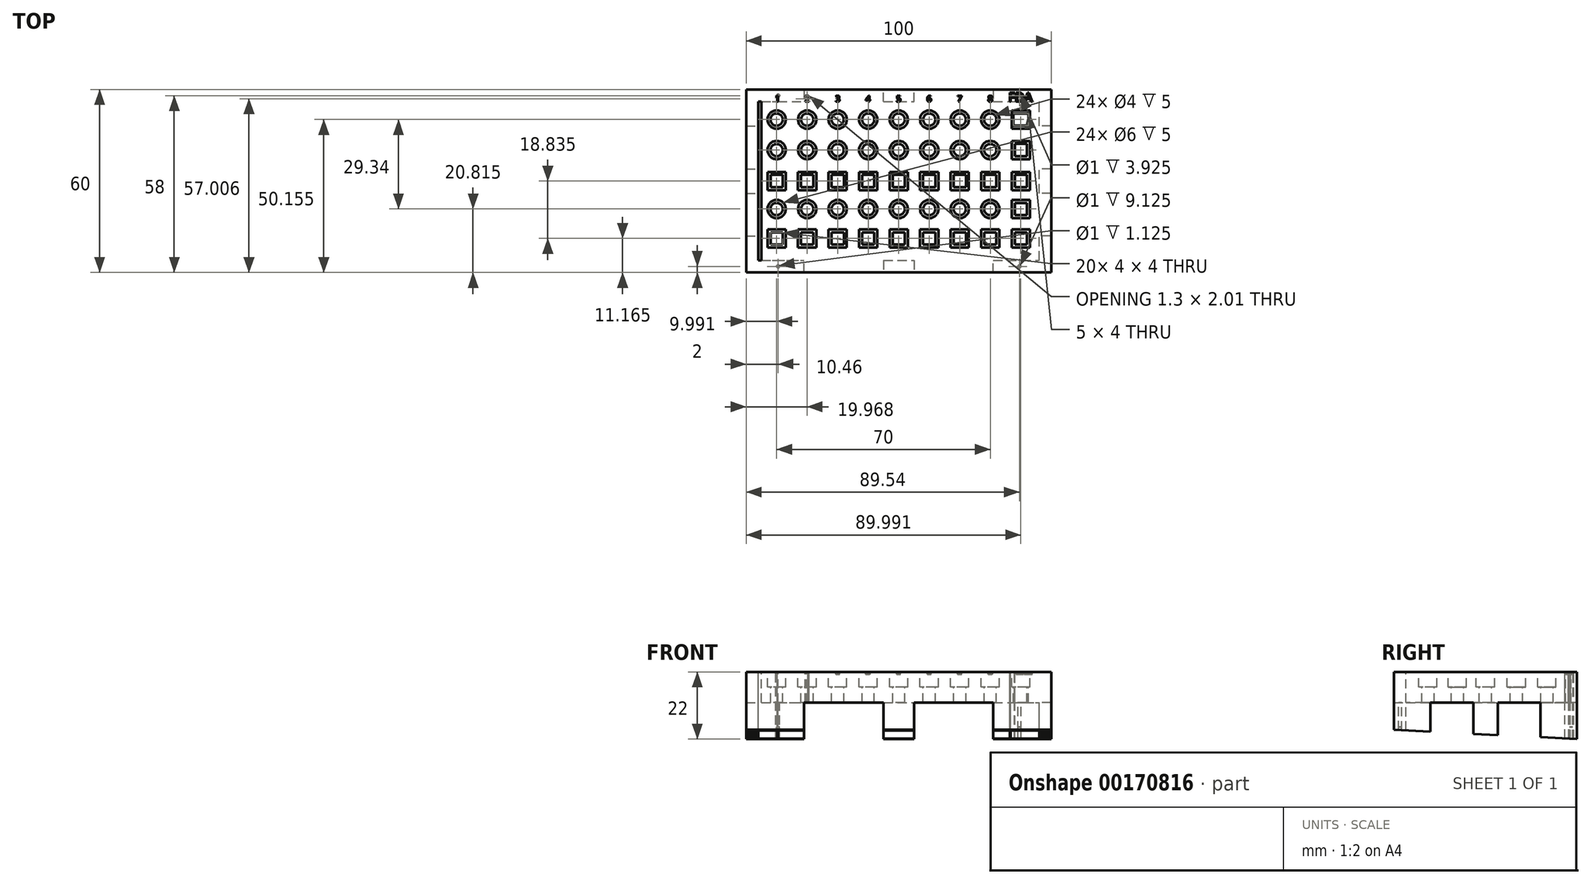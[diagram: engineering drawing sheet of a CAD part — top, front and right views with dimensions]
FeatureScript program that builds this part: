
annotation { "Feature Type Name" : "Feature", "Feature Type Description" : "" }
export const myFeature = defineFeature(function(context is Context, id is Id, definition is map)
    precondition{}
    {
        {
            var Q0;
            Q0=qCreatedBy(makeId("Top.planeOp"),FACE);
            var sketch = newSketch(context, id + "F0", { "sketchPlane" : qUnion([Q0])});
            skLineSegment(sketch, "E0.bottom", {"start": v(0, 0) * mm, "end": v(100, 0) * mm});
            skLineSegment(sketch, "E0.top", {"start": v(0, 60) * mm, "end": v(100, 60) * mm});
            skLineSegment(sketch, "E0.left", {"start": v(0, 0) * mm, "end": v(0, 60) * mm});
            skLineSegment(sketch, "E0.right", {"start": v(100, 0) * mm, "end": v(100, 60) * mm});
            skLineSegment(sketch, "E1.top", {"start": v(0, 88.72) * mm, "end": v(100, 88.72) * mm, "construction": true});
            skLineSegment(sketch, "E1.left", {"start": v(0, 60) * mm, "end": v(0, 88.72) * mm, "construction": true});
            skLineSegment(sketch, "E1.right", {"start": v(100, 60) * mm, "end": v(100, 88.72) * mm, "construction": true});
            skLineSegment(sketch, "E2", {"start": v(5, 88.72) * mm, "end": v(5, 60) * mm, "construction": true});
            skCircle(sketch, "E3", {"center": v(10, 20.81) * mm, "radius": 3 * mm});
            skLineSegment(sketch, "E4.0", {"start": v(4, 56) * mm, "end": v(96, 56) * mm});
            skLineSegment(sketch, "E4.2", {"start": v(4, 4) * mm, "end": v(96, 4) * mm});
            skLineSegment(sketch, "E4.3", {"start": v(96, 4) * mm, "end": v(96, 56) * mm});
            skLineSegment(sketch, "E5.bottom", {"start": v(5, 56) * mm, "end": v(4, 56) * mm});
            skLineSegment(sketch, "E5.top", {"start": v(5, 4.3) * mm, "end": v(4, 4.3) * mm, "construction": true});
            skLineSegment(sketch, "E5.left", {"start": v(5, 56) * mm, "end": v(5, 4.3) * mm});
            skLineSegment(sketch, "E5.right", {"start": v(4, 56) * mm, "end": v(4, 4.3) * mm});
            skPoint(sketch, "E5.middle", {"position": v(4.5, 30.15) * mm});
            skCircle(sketch, "E6", {"center": v(10, 50.15) * mm, "radius": 3 * mm});
            skCircle(sketch, "E7", {"center": v(10, 40.15) * mm, "radius": 3 * mm});
            skLineSegment(sketch, "E8.bottom", {"start": v(13, 14.17) * mm, "end": v(7, 14.17) * mm});
            skLineSegment(sketch, "E8.top", {"start": v(13, 8.17) * mm, "end": v(7, 8.17) * mm});
            skLineSegment(sketch, "E8.left", {"start": v(13, 14.17) * mm, "end": v(13, 8.17) * mm});
            skLineSegment(sketch, "E8.right", {"start": v(7, 14.17) * mm, "end": v(7, 8.17) * mm});
            skLineSegment(sketch, "E9.bottom", {"start": v(12, 13.17) * mm, "end": v(8, 13.17) * mm});
            skLineSegment(sketch, "E9.top", {"start": v(12, 9.17) * mm, "end": v(8, 9.17) * mm});
            skLineSegment(sketch, "E9.left", {"start": v(12, 13.17) * mm, "end": v(12, 9.17) * mm});
            skLineSegment(sketch, "E9.right", {"start": v(8, 13.17) * mm, "end": v(8, 9.17) * mm});
            skPoint(sketch, "E9.middle", {"position": v(10, 11.17) * mm});
            skCircle(sketch, "E10", {"center": v(10, 50.15) * mm, "radius": 2 * mm});
            skCircle(sketch, "E11", {"center": v(10, 40.15) * mm, "radius": 2 * mm});
            skCircle(sketch, "E12", {"center": v(10, 20.81) * mm, "radius": 2 * mm});
            skLineSegment(sketch, "E13", {"start": v(4.5, 56) * mm, "end": v(4.5, 4.3) * mm, "construction": true});
            skLineSegment(sketch, "E14", {"start": v(10, 4) * mm, "end": v(10, 56) * mm, "construction": true});
            skLineSegment(sketch, "E15.bottom", {"start": v(12, 32) * mm, "end": v(8, 32) * mm});
            skLineSegment(sketch, "E15.top", {"start": v(12, 28) * mm, "end": v(8, 28) * mm});
            skLineSegment(sketch, "E15.left", {"start": v(12, 32) * mm, "end": v(12, 28) * mm});
            skLineSegment(sketch, "E15.right", {"start": v(8, 32) * mm, "end": v(8, 28) * mm});
            skPoint(sketch, "E15.middle", {"position": v(10, 30) * mm});
            skLineSegment(sketch, "E16.bottom", {"start": v(13, 33) * mm, "end": v(7, 33) * mm});
            skLineSegment(sketch, "E16.top", {"start": v(13, 27) * mm, "end": v(7, 27) * mm});
            skLineSegment(sketch, "E16.left", {"start": v(13, 33) * mm, "end": v(13, 27) * mm});
            skLineSegment(sketch, "E16.right", {"start": v(7, 33) * mm, "end": v(7, 27) * mm});
            skLineSegment(sketch, "E17.1.0.0", {"start": v(14, 56) * mm, "end": v(14, 4.3) * mm});
            skLineSegment(sketch, "E17.1.0.1", {"start": v(14.5, 56) * mm, "end": v(14.5, 4.3) * mm, "construction": true});
            skLineSegment(sketch, "E17.1.0.2", {"start": v(15, 56) * mm, "end": v(15, 4.3) * mm});
            skLineSegment(sketch, "E17.2.0.0", {"start": v(24, 56) * mm, "end": v(24, 4.3) * mm});
            skLineSegment(sketch, "E17.2.0.1", {"start": v(24.5, 56) * mm, "end": v(24.5, 4.3) * mm, "construction": true});
            skLineSegment(sketch, "E17.2.0.2", {"start": v(25, 56) * mm, "end": v(25, 4.3) * mm});
            skLineSegment(sketch, "E17.3.0.0", {"start": v(34, 56) * mm, "end": v(34, 4.3) * mm});
            skLineSegment(sketch, "E17.3.0.1", {"start": v(34.5, 56) * mm, "end": v(34.5, 4.3) * mm, "construction": true});
            skLineSegment(sketch, "E17.3.0.2", {"start": v(35, 56) * mm, "end": v(35, 4.3) * mm});
            skLineSegment(sketch, "E17.4.0.0", {"start": v(44, 56) * mm, "end": v(44, 4.3) * mm});
            skLineSegment(sketch, "E17.4.0.1", {"start": v(44.5, 56) * mm, "end": v(44.5, 4.3) * mm, "construction": true});
            skLineSegment(sketch, "E17.4.0.2", {"start": v(45, 56) * mm, "end": v(45, 4.3) * mm});
            skLineSegment(sketch, "E17.5.0.0", {"start": v(54, 56) * mm, "end": v(54, 4.3) * mm});
            skLineSegment(sketch, "E17.5.0.1", {"start": v(54.5, 56) * mm, "end": v(54.5, 4.3) * mm, "construction": true});
            skLineSegment(sketch, "E17.5.0.2", {"start": v(55, 56) * mm, "end": v(55, 4.3) * mm});
            skLineSegment(sketch, "E17.6.0.0", {"start": v(64, 56) * mm, "end": v(64, 4.3) * mm});
            skLineSegment(sketch, "E17.6.0.1", {"start": v(64.5, 56) * mm, "end": v(64.5, 4.3) * mm, "construction": true});
            skLineSegment(sketch, "E17.6.0.2", {"start": v(65, 56) * mm, "end": v(65, 4.3) * mm});
            skLineSegment(sketch, "E17.7.0.0", {"start": v(74, 56) * mm, "end": v(74, 4.3) * mm});
            skLineSegment(sketch, "E17.7.0.1", {"start": v(74.5, 56) * mm, "end": v(74.5, 4.3) * mm, "construction": true});
            skLineSegment(sketch, "E17.7.0.2", {"start": v(75, 56) * mm, "end": v(75, 4.3) * mm});
            skLineSegment(sketch, "E17.8.0.0", {"start": v(84, 56) * mm, "end": v(84, 4.3) * mm});
            skLineSegment(sketch, "E17.8.0.1", {"start": v(84.5, 56) * mm, "end": v(84.5, 4.3) * mm, "construction": true});
            skLineSegment(sketch, "E17.8.0.2", {"start": v(85, 56) * mm, "end": v(85, 4.3) * mm});
            skLineSegment(sketch, "E17.direction1", {"start": v(4, 4.3) * mm, "end": v(14, 4.3) * mm, "construction": true});
            skLineSegment(sketch, "E18.1.0.0", {"start": v(22, 9.17) * mm, "end": v(18, 9.17) * mm});
            skPoint(sketch, "E18.1.0.1", {"position": v(20, 30) * mm});
            skCircle(sketch, "E18.1.0.2", {"center": v(20, 20.81) * mm, "radius": 3 * mm});
            skLineSegment(sketch, "E18.1.0.3", {"start": v(23, 8.17) * mm, "end": v(17, 8.17) * mm});
            skPoint(sketch, "E18.1.0.4", {"position": v(20, 11.17) * mm});
            skLineSegment(sketch, "E18.1.0.5", {"start": v(18, 13.17) * mm, "end": v(18, 9.17) * mm});
            skLineSegment(sketch, "E18.1.0.6", {"start": v(23, 33) * mm, "end": v(17, 33) * mm});
            skLineSegment(sketch, "E18.1.0.7", {"start": v(23, 33) * mm, "end": v(23, 27) * mm});
            skLineSegment(sketch, "E18.1.0.8", {"start": v(17, 33) * mm, "end": v(17, 27) * mm});
            skLineSegment(sketch, "E18.1.0.9", {"start": v(22, 32) * mm, "end": v(22, 28) * mm});
            skLineSegment(sketch, "E18.1.0.10", {"start": v(22, 13.17) * mm, "end": v(22, 9.17) * mm});
            skLineSegment(sketch, "E18.1.0.11", {"start": v(23, 14.17) * mm, "end": v(17, 14.17) * mm});
            skCircle(sketch, "E18.1.0.12", {"center": v(20, 50.15) * mm, "radius": 2 * mm});
            skLineSegment(sketch, "E18.1.0.13", {"start": v(17, 14.17) * mm, "end": v(17, 8.17) * mm});
            skCircle(sketch, "E18.1.0.14", {"center": v(20, 50.15) * mm, "radius": 3 * mm});
            skLineSegment(sketch, "E18.1.0.15", {"start": v(18, 32) * mm, "end": v(18, 28) * mm});
            skCircle(sketch, "E18.1.0.16", {"center": v(20, 40.15) * mm, "radius": 2 * mm});
            skLineSegment(sketch, "E18.1.0.17", {"start": v(22, 13.17) * mm, "end": v(18, 13.17) * mm});
            skLineSegment(sketch, "E18.1.0.18", {"start": v(22, 32) * mm, "end": v(18, 32) * mm});
            skLineSegment(sketch, "E18.1.0.19", {"start": v(23, 14.17) * mm, "end": v(23, 8.17) * mm});
            skCircle(sketch, "E18.1.0.20", {"center": v(20, 20.81) * mm, "radius": 2 * mm});
            skCircle(sketch, "E18.1.0.21", {"center": v(20, 40.15) * mm, "radius": 3 * mm});
            skPoint(sketch, "E18.1.0.22", {"position": v(20, 30) * mm});
            skLineSegment(sketch, "E18.1.0.23", {"start": v(22, 28) * mm, "end": v(18, 28) * mm});
            skLineSegment(sketch, "E18.1.0.24", {"start": v(23, 27) * mm, "end": v(17, 27) * mm});
            skLineSegment(sketch, "E18.2.0.0", {"start": v(32, 9.17) * mm, "end": v(28, 9.17) * mm});
            skPoint(sketch, "E18.2.0.1", {"position": v(30, 30) * mm});
            skCircle(sketch, "E18.2.0.2", {"center": v(30, 20.81) * mm, "radius": 3 * mm});
            skLineSegment(sketch, "E18.2.0.3", {"start": v(33, 8.17) * mm, "end": v(27, 8.17) * mm});
            skPoint(sketch, "E18.2.0.4", {"position": v(30, 11.17) * mm});
            skLineSegment(sketch, "E18.2.0.5", {"start": v(28, 13.17) * mm, "end": v(28, 9.17) * mm});
            skLineSegment(sketch, "E18.2.0.6", {"start": v(33, 33) * mm, "end": v(27, 33) * mm});
            skLineSegment(sketch, "E18.2.0.7", {"start": v(33, 33) * mm, "end": v(33, 27) * mm});
            skLineSegment(sketch, "E18.2.0.8", {"start": v(27, 33) * mm, "end": v(27, 27) * mm});
            skLineSegment(sketch, "E18.2.0.9", {"start": v(32, 32) * mm, "end": v(32, 28) * mm});
            skLineSegment(sketch, "E18.2.0.10", {"start": v(32, 13.17) * mm, "end": v(32, 9.17) * mm});
            skLineSegment(sketch, "E18.2.0.11", {"start": v(33, 14.17) * mm, "end": v(27, 14.17) * mm});
            skCircle(sketch, "E18.2.0.12", {"center": v(30, 50.15) * mm, "radius": 2 * mm});
            skLineSegment(sketch, "E18.2.0.13", {"start": v(27, 14.17) * mm, "end": v(27, 8.17) * mm});
            skCircle(sketch, "E18.2.0.14", {"center": v(30, 50.15) * mm, "radius": 3 * mm});
            skLineSegment(sketch, "E18.2.0.15", {"start": v(28, 32) * mm, "end": v(28, 28) * mm});
            skCircle(sketch, "E18.2.0.16", {"center": v(30, 40.15) * mm, "radius": 2 * mm});
            skLineSegment(sketch, "E18.2.0.17", {"start": v(32, 13.17) * mm, "end": v(28, 13.17) * mm});
            skLineSegment(sketch, "E18.2.0.18", {"start": v(32, 32) * mm, "end": v(28, 32) * mm});
            skLineSegment(sketch, "E18.2.0.19", {"start": v(33, 14.17) * mm, "end": v(33, 8.17) * mm});
            skCircle(sketch, "E18.2.0.20", {"center": v(30, 20.81) * mm, "radius": 2 * mm});
            skCircle(sketch, "E18.2.0.21", {"center": v(30, 40.15) * mm, "radius": 3 * mm});
            skPoint(sketch, "E18.2.0.22", {"position": v(30, 30) * mm});
            skLineSegment(sketch, "E18.2.0.23", {"start": v(32, 28) * mm, "end": v(28, 28) * mm});
            skLineSegment(sketch, "E18.2.0.24", {"start": v(33, 27) * mm, "end": v(27, 27) * mm});
            skLineSegment(sketch, "E18.3.0.0", {"start": v(42, 9.17) * mm, "end": v(38, 9.17) * mm});
            skPoint(sketch, "E18.3.0.1", {"position": v(40, 30) * mm});
            skCircle(sketch, "E18.3.0.2", {"center": v(40, 20.81) * mm, "radius": 3 * mm});
            skLineSegment(sketch, "E18.3.0.3", {"start": v(43, 8.17) * mm, "end": v(37, 8.17) * mm});
            skPoint(sketch, "E18.3.0.4", {"position": v(40, 11.17) * mm});
            skLineSegment(sketch, "E18.3.0.5", {"start": v(38, 13.17) * mm, "end": v(38, 9.17) * mm});
            skLineSegment(sketch, "E18.3.0.6", {"start": v(43, 33) * mm, "end": v(37, 33) * mm});
            skLineSegment(sketch, "E18.3.0.7", {"start": v(43, 33) * mm, "end": v(43, 27) * mm});
            skLineSegment(sketch, "E18.3.0.8", {"start": v(37, 33) * mm, "end": v(37, 27) * mm});
            skLineSegment(sketch, "E18.3.0.9", {"start": v(42, 32) * mm, "end": v(42, 28) * mm});
            skLineSegment(sketch, "E18.3.0.10", {"start": v(42, 13.17) * mm, "end": v(42, 9.17) * mm});
            skLineSegment(sketch, "E18.3.0.11", {"start": v(43, 14.17) * mm, "end": v(37, 14.17) * mm});
            skCircle(sketch, "E18.3.0.12", {"center": v(40, 50.15) * mm, "radius": 2 * mm});
            skLineSegment(sketch, "E18.3.0.13", {"start": v(37, 14.17) * mm, "end": v(37, 8.17) * mm});
            skCircle(sketch, "E18.3.0.14", {"center": v(40, 50.15) * mm, "radius": 3 * mm});
            skLineSegment(sketch, "E18.3.0.15", {"start": v(38, 32) * mm, "end": v(38, 28) * mm});
            skCircle(sketch, "E18.3.0.16", {"center": v(40, 40.15) * mm, "radius": 2 * mm});
            skLineSegment(sketch, "E18.3.0.17", {"start": v(42, 13.17) * mm, "end": v(38, 13.17) * mm});
            skLineSegment(sketch, "E18.3.0.18", {"start": v(42, 32) * mm, "end": v(38, 32) * mm});
            skLineSegment(sketch, "E18.3.0.19", {"start": v(43, 14.17) * mm, "end": v(43, 8.17) * mm});
            skCircle(sketch, "E18.3.0.20", {"center": v(40, 20.81) * mm, "radius": 2 * mm});
            skCircle(sketch, "E18.3.0.21", {"center": v(40, 40.15) * mm, "radius": 3 * mm});
            skPoint(sketch, "E18.3.0.22", {"position": v(40, 30) * mm});
            skLineSegment(sketch, "E18.3.0.23", {"start": v(42, 28) * mm, "end": v(38, 28) * mm});
            skLineSegment(sketch, "E18.3.0.24", {"start": v(43, 27) * mm, "end": v(37, 27) * mm});
            skLineSegment(sketch, "E18.4.0.0", {"start": v(52, 9.17) * mm, "end": v(48, 9.17) * mm});
            skPoint(sketch, "E18.4.0.1", {"position": v(50, 30) * mm});
            skCircle(sketch, "E18.4.0.2", {"center": v(50, 20.81) * mm, "radius": 3 * mm});
            skLineSegment(sketch, "E18.4.0.3", {"start": v(53, 8.17) * mm, "end": v(47, 8.17) * mm});
            skPoint(sketch, "E18.4.0.4", {"position": v(50, 11.17) * mm});
            skLineSegment(sketch, "E18.4.0.5", {"start": v(48, 13.17) * mm, "end": v(48, 9.17) * mm});
            skLineSegment(sketch, "E18.4.0.6", {"start": v(53, 33) * mm, "end": v(47, 33) * mm});
            skLineSegment(sketch, "E18.4.0.7", {"start": v(53, 33) * mm, "end": v(53, 27) * mm});
            skLineSegment(sketch, "E18.4.0.8", {"start": v(47, 33) * mm, "end": v(47, 27) * mm});
            skLineSegment(sketch, "E18.4.0.9", {"start": v(52, 32) * mm, "end": v(52, 28) * mm});
            skLineSegment(sketch, "E18.4.0.10", {"start": v(52, 13.17) * mm, "end": v(52, 9.17) * mm});
            skLineSegment(sketch, "E18.4.0.11", {"start": v(53, 14.17) * mm, "end": v(47, 14.17) * mm});
            skCircle(sketch, "E18.4.0.12", {"center": v(50, 50.15) * mm, "radius": 2 * mm});
            skLineSegment(sketch, "E18.4.0.13", {"start": v(47, 14.17) * mm, "end": v(47, 8.17) * mm});
            skCircle(sketch, "E18.4.0.14", {"center": v(50, 50.15) * mm, "radius": 3 * mm});
            skLineSegment(sketch, "E18.4.0.15", {"start": v(48, 32) * mm, "end": v(48, 28) * mm});
            skCircle(sketch, "E18.4.0.16", {"center": v(50, 40.15) * mm, "radius": 2 * mm});
            skLineSegment(sketch, "E18.4.0.17", {"start": v(52, 13.17) * mm, "end": v(48, 13.17) * mm});
            skLineSegment(sketch, "E18.4.0.18", {"start": v(52, 32) * mm, "end": v(48, 32) * mm});
            skLineSegment(sketch, "E18.4.0.19", {"start": v(53, 14.17) * mm, "end": v(53, 8.17) * mm});
            skCircle(sketch, "E18.4.0.20", {"center": v(50, 20.81) * mm, "radius": 2 * mm});
            skCircle(sketch, "E18.4.0.21", {"center": v(50, 40.15) * mm, "radius": 3 * mm});
            skPoint(sketch, "E18.4.0.22", {"position": v(50, 30) * mm});
            skLineSegment(sketch, "E18.4.0.23", {"start": v(52, 28) * mm, "end": v(48, 28) * mm});
            skLineSegment(sketch, "E18.4.0.24", {"start": v(53, 27) * mm, "end": v(47, 27) * mm});
            skLineSegment(sketch, "E18.5.0.0", {"start": v(62, 9.17) * mm, "end": v(58, 9.17) * mm});
            skPoint(sketch, "E18.5.0.1", {"position": v(60, 30) * mm});
            skCircle(sketch, "E18.5.0.2", {"center": v(60, 20.81) * mm, "radius": 3 * mm});
            skLineSegment(sketch, "E18.5.0.3", {"start": v(63, 8.17) * mm, "end": v(57, 8.17) * mm});
            skPoint(sketch, "E18.5.0.4", {"position": v(60, 11.17) * mm});
            skLineSegment(sketch, "E18.5.0.5", {"start": v(58, 13.17) * mm, "end": v(58, 9.17) * mm});
            skLineSegment(sketch, "E18.5.0.6", {"start": v(63, 33) * mm, "end": v(57, 33) * mm});
            skLineSegment(sketch, "E18.5.0.7", {"start": v(63, 33) * mm, "end": v(63, 27) * mm});
            skLineSegment(sketch, "E18.5.0.8", {"start": v(57, 33) * mm, "end": v(57, 27) * mm});
            skLineSegment(sketch, "E18.5.0.9", {"start": v(62, 32) * mm, "end": v(62, 28) * mm});
            skLineSegment(sketch, "E18.5.0.10", {"start": v(62, 13.17) * mm, "end": v(62, 9.17) * mm});
            skLineSegment(sketch, "E18.5.0.11", {"start": v(63, 14.17) * mm, "end": v(57, 14.17) * mm});
            skCircle(sketch, "E18.5.0.12", {"center": v(60, 50.15) * mm, "radius": 2 * mm});
            skLineSegment(sketch, "E18.5.0.13", {"start": v(57, 14.17) * mm, "end": v(57, 8.17) * mm});
            skCircle(sketch, "E18.5.0.14", {"center": v(60, 50.15) * mm, "radius": 3 * mm});
            skLineSegment(sketch, "E18.5.0.15", {"start": v(58, 32) * mm, "end": v(58, 28) * mm});
            skCircle(sketch, "E18.5.0.16", {"center": v(60, 40.15) * mm, "radius": 2 * mm});
            skLineSegment(sketch, "E18.5.0.17", {"start": v(62, 13.17) * mm, "end": v(58, 13.17) * mm});
            skLineSegment(sketch, "E18.5.0.18", {"start": v(62, 32) * mm, "end": v(58, 32) * mm});
            skLineSegment(sketch, "E18.5.0.19", {"start": v(63, 14.17) * mm, "end": v(63, 8.17) * mm});
            skCircle(sketch, "E18.5.0.20", {"center": v(60, 20.81) * mm, "radius": 2 * mm});
            skCircle(sketch, "E18.5.0.21", {"center": v(60, 40.15) * mm, "radius": 3 * mm});
            skPoint(sketch, "E18.5.0.22", {"position": v(60, 30) * mm});
            skLineSegment(sketch, "E18.5.0.23", {"start": v(62, 28) * mm, "end": v(58, 28) * mm});
            skLineSegment(sketch, "E18.5.0.24", {"start": v(63, 27) * mm, "end": v(57, 27) * mm});
            skLineSegment(sketch, "E18.6.0.0", {"start": v(72, 9.17) * mm, "end": v(68, 9.17) * mm});
            skPoint(sketch, "E18.6.0.1", {"position": v(70, 30) * mm});
            skCircle(sketch, "E18.6.0.2", {"center": v(70, 20.81) * mm, "radius": 3 * mm});
            skLineSegment(sketch, "E18.6.0.3", {"start": v(73, 8.17) * mm, "end": v(67, 8.17) * mm});
            skPoint(sketch, "E18.6.0.4", {"position": v(70, 11.17) * mm});
            skLineSegment(sketch, "E18.6.0.5", {"start": v(68, 13.17) * mm, "end": v(68, 9.17) * mm});
            skLineSegment(sketch, "E18.6.0.6", {"start": v(73, 33) * mm, "end": v(67, 33) * mm});
            skLineSegment(sketch, "E18.6.0.7", {"start": v(73, 33) * mm, "end": v(73, 27) * mm});
            skLineSegment(sketch, "E18.6.0.8", {"start": v(67, 33) * mm, "end": v(67, 27) * mm});
            skLineSegment(sketch, "E18.6.0.9", {"start": v(72, 32) * mm, "end": v(72, 28) * mm});
            skLineSegment(sketch, "E18.6.0.10", {"start": v(72, 13.17) * mm, "end": v(72, 9.17) * mm});
            skLineSegment(sketch, "E18.6.0.11", {"start": v(73, 14.17) * mm, "end": v(67, 14.17) * mm});
            skCircle(sketch, "E18.6.0.12", {"center": v(70, 50.15) * mm, "radius": 2 * mm});
            skLineSegment(sketch, "E18.6.0.13", {"start": v(67, 14.17) * mm, "end": v(67, 8.17) * mm});
            skCircle(sketch, "E18.6.0.14", {"center": v(70, 50.15) * mm, "radius": 3 * mm});
            skLineSegment(sketch, "E18.6.0.15", {"start": v(68, 32) * mm, "end": v(68, 28) * mm});
            skCircle(sketch, "E18.6.0.16", {"center": v(70, 40.15) * mm, "radius": 2 * mm});
            skLineSegment(sketch, "E18.6.0.17", {"start": v(72, 13.17) * mm, "end": v(68, 13.17) * mm});
            skLineSegment(sketch, "E18.6.0.18", {"start": v(72, 32) * mm, "end": v(68, 32) * mm});
            skLineSegment(sketch, "E18.6.0.19", {"start": v(73, 14.17) * mm, "end": v(73, 8.17) * mm});
            skCircle(sketch, "E18.6.0.20", {"center": v(70, 20.81) * mm, "radius": 2 * mm});
            skCircle(sketch, "E18.6.0.21", {"center": v(70, 40.15) * mm, "radius": 3 * mm});
            skPoint(sketch, "E18.6.0.22", {"position": v(70, 30) * mm});
            skLineSegment(sketch, "E18.6.0.23", {"start": v(72, 28) * mm, "end": v(68, 28) * mm});
            skLineSegment(sketch, "E18.6.0.24", {"start": v(73, 27) * mm, "end": v(67, 27) * mm});
            skLineSegment(sketch, "E18.7.0.0", {"start": v(82, 9.17) * mm, "end": v(78, 9.17) * mm});
            skPoint(sketch, "E18.7.0.1", {"position": v(80, 30) * mm});
            skCircle(sketch, "E18.7.0.2", {"center": v(80, 20.81) * mm, "radius": 3 * mm});
            skLineSegment(sketch, "E18.7.0.3", {"start": v(83, 8.17) * mm, "end": v(77, 8.17) * mm});
            skPoint(sketch, "E18.7.0.4", {"position": v(80, 11.17) * mm});
            skLineSegment(sketch, "E18.7.0.5", {"start": v(78, 13.17) * mm, "end": v(78, 9.17) * mm});
            skLineSegment(sketch, "E18.7.0.6", {"start": v(83, 33) * mm, "end": v(77, 33) * mm});
            skLineSegment(sketch, "E18.7.0.7", {"start": v(83, 33) * mm, "end": v(83, 27) * mm});
            skLineSegment(sketch, "E18.7.0.8", {"start": v(77, 33) * mm, "end": v(77, 27) * mm});
            skLineSegment(sketch, "E18.7.0.9", {"start": v(82, 32) * mm, "end": v(82, 28) * mm});
            skLineSegment(sketch, "E18.7.0.10", {"start": v(82, 13.17) * mm, "end": v(82, 9.17) * mm});
            skLineSegment(sketch, "E18.7.0.11", {"start": v(83, 14.17) * mm, "end": v(77, 14.17) * mm});
            skCircle(sketch, "E18.7.0.12", {"center": v(80, 50.15) * mm, "radius": 2 * mm});
            skLineSegment(sketch, "E18.7.0.13", {"start": v(77, 14.17) * mm, "end": v(77, 8.17) * mm});
            skCircle(sketch, "E18.7.0.14", {"center": v(80, 50.15) * mm, "radius": 3 * mm});
            skLineSegment(sketch, "E18.7.0.15", {"start": v(78, 32) * mm, "end": v(78, 28) * mm});
            skCircle(sketch, "E18.7.0.16", {"center": v(80, 40.15) * mm, "radius": 2 * mm});
            skLineSegment(sketch, "E18.7.0.17", {"start": v(82, 13.17) * mm, "end": v(78, 13.17) * mm});
            skLineSegment(sketch, "E18.7.0.18", {"start": v(82, 32) * mm, "end": v(78, 32) * mm});
            skLineSegment(sketch, "E18.7.0.19", {"start": v(83, 14.17) * mm, "end": v(83, 8.17) * mm});
            skCircle(sketch, "E18.7.0.20", {"center": v(80, 20.81) * mm, "radius": 2 * mm});
            skCircle(sketch, "E18.7.0.21", {"center": v(80, 40.15) * mm, "radius": 3 * mm});
            skPoint(sketch, "E18.7.0.22", {"position": v(80, 30) * mm});
            skLineSegment(sketch, "E18.7.0.23", {"start": v(82, 28) * mm, "end": v(78, 28) * mm});
            skLineSegment(sketch, "E18.7.0.24", {"start": v(83, 27) * mm, "end": v(77, 27) * mm});
            skLineSegment(sketch, "E18.direction1", {"start": v(7, 8.17) * mm, "end": v(17, 8.17) * mm, "construction": true});
            skText(sketch, "E19", { "text": "1", "fontName": "OpenSans-Regular.ttf"});
            skText(sketch, "E20", { "text": "2", "fontName": "OpenSans-Regular.ttf"});
            skText(sketch, "E21", { "text": "3", "fontName": "OpenSans-Regular.ttf"});
            skText(sketch, "E22", { "text": "4", "fontName": "OpenSans-Regular.ttf"});
            skText(sketch, "E23", { "text": "5", "fontName": "OpenSans-Regular.ttf"});
            skText(sketch, "E24", { "text": "6", "fontName": "OpenSans-Regular.ttf"});
            skText(sketch, "E25", { "text": "7\n", "fontName": "OpenSans-Regular.ttf"});
            skText(sketch, "E26", { "text": "8", "fontName": "OpenSans-Regular.ttf"});
            skLineSegment(sketch, "E27", {"start": v(10, 56) * mm, "end": v(20, 56) * mm, "construction": true});
            skLineSegment(sketch, "E28", {"start": v(20, 56) * mm, "end": v(30, 56) * mm, "construction": true});
            skLineSegment(sketch, "E29", {"start": v(30, 56) * mm, "end": v(40, 56) * mm, "construction": true});
            skLineSegment(sketch, "E30", {"start": v(40, 56) * mm, "end": v(50, 56) * mm, "construction": true});
            skLineSegment(sketch, "E31", {"start": v(50, 56) * mm, "end": v(60, 56) * mm, "construction": true});
            skLineSegment(sketch, "E32", {"start": v(60, 56) * mm, "end": v(70, 56) * mm, "construction": true});
            skLineSegment(sketch, "E33", {"start": v(70, 56) * mm, "end": v(80, 56) * mm, "construction": true});
            skLineSegment(sketch, "E34", {"start": v(80, 56) * mm, "end": v(90, 56) * mm, "construction": true});
            skLineSegment(sketch, "E35", {"start": v(14, 56) * mm, "end": v(15, 56) * mm});
            skLineSegment(sketch, "E36", {"start": v(14, 4.3) * mm, "end": v(14, 4) * mm});
            skLineSegment(sketch, "E37", {"start": v(14, 4) * mm, "end": v(15, 4) * mm});
            skLineSegment(sketch, "E38", {"start": v(15, 4) * mm, "end": v(15, 4.3) * mm});
            skLineSegment(sketch, "E39", {"start": v(24, 4.3) * mm, "end": v(24, 4) * mm});
            skLineSegment(sketch, "E40", {"start": v(24, 4) * mm, "end": v(25, 4) * mm});
            skLineSegment(sketch, "E41", {"start": v(25, 4.3) * mm, "end": v(25, 4) * mm});
            skLineSegment(sketch, "E42", {"start": v(34, 4.3) * mm, "end": v(34, 4) * mm});
            skLineSegment(sketch, "E43.top", {"start": v(34, 4) * mm, "end": v(35, 4) * mm});
            skLineSegment(sketch, "E43.right", {"start": v(35, 4.3) * mm, "end": v(35, 4) * mm});
            skLineSegment(sketch, "E44.top", {"start": v(44, 4) * mm, "end": v(45, 4) * mm});
            skLineSegment(sketch, "E44.left", {"start": v(44, 4.3) * mm, "end": v(44, 4) * mm});
            skLineSegment(sketch, "E44.right", {"start": v(45, 4.3) * mm, "end": v(45, 4) * mm});
            skLineSegment(sketch, "E45.top", {"start": v(54, 4) * mm, "end": v(55, 4) * mm});
            skLineSegment(sketch, "E45.left", {"start": v(54, 4.3) * mm, "end": v(54, 4) * mm});
            skLineSegment(sketch, "E45.right", {"start": v(55, 4.3) * mm, "end": v(55, 4) * mm});
            skLineSegment(sketch, "E46.top", {"start": v(64, 4) * mm, "end": v(65, 4) * mm});
            skLineSegment(sketch, "E46.left", {"start": v(64, 4.3) * mm, "end": v(64, 4) * mm});
            skLineSegment(sketch, "E46.right", {"start": v(65, 4.3) * mm, "end": v(65, 4) * mm});
            skLineSegment(sketch, "E47.top", {"start": v(74, 4) * mm, "end": v(75, 4) * mm});
            skLineSegment(sketch, "E47.left", {"start": v(74, 4.3) * mm, "end": v(74, 4) * mm});
            skLineSegment(sketch, "E47.right", {"start": v(75, 4.3) * mm, "end": v(75, 4) * mm});
            skLineSegment(sketch, "E48.top", {"start": v(84, 4) * mm, "end": v(85, 4) * mm});
            skLineSegment(sketch, "E48.left", {"start": v(84, 4.3) * mm, "end": v(84, 4) * mm});
            skLineSegment(sketch, "E48.right", {"start": v(85, 4.3) * mm, "end": v(85, 4) * mm});
            skLineSegment(sketch, "E49", {"start": v(4, 4.3) * mm, "end": v(4, 4) * mm});
            skLineSegment(sketch, "E50", {"start": v(5, 4.3) * mm, "end": v(5, 4) * mm});
            skLineSegment(sketch, "E51", {"start": v(90, 56) * mm, "end": v(90, 4) * mm, "construction": true});
            skLineSegment(sketch, "E52.bottom", {"start": v(92, 13.17) * mm, "end": v(88, 13.17) * mm});
            skLineSegment(sketch, "E52.top", {"start": v(92, 9.17) * mm, "end": v(88, 9.17) * mm});
            skLineSegment(sketch, "E52.left", {"start": v(92, 13.17) * mm, "end": v(92, 9.17) * mm});
            skLineSegment(sketch, "E52.right", {"start": v(88, 13.17) * mm, "end": v(88, 9.17) * mm});
            skPoint(sketch, "E52.middle", {"position": v(90, 11.17) * mm});
            skPoint(sketch, "E52.middle.positionSnap0", {"position": v(83, 11.17) * mm});
            skPoint(sketch, "E52.centerSnap0", {"position": v(83, 11.17) * mm});
            skLineSegment(sketch, "E53.bottom", {"start": v(93, 14.17) * mm, "end": v(87, 14.17) * mm});
            skLineSegment(sketch, "E53.top", {"start": v(93, 8.17) * mm, "end": v(87, 8.17) * mm});
            skLineSegment(sketch, "E53.left", {"start": v(93, 14.17) * mm, "end": v(93, 8.17) * mm});
            skLineSegment(sketch, "E53.right", {"start": v(87, 14.17) * mm, "end": v(87, 8.17) * mm});
            skLineSegment(sketch, "E54.bottom", {"start": v(92, 22.81) * mm, "end": v(88, 22.81) * mm});
            skLineSegment(sketch, "E54.top", {"start": v(92, 18.81) * mm, "end": v(88, 18.81) * mm});
            skLineSegment(sketch, "E54.left", {"start": v(92, 22.81) * mm, "end": v(92, 18.81) * mm});
            skLineSegment(sketch, "E54.right", {"start": v(88, 22.81) * mm, "end": v(88, 18.81) * mm});
            skPoint(sketch, "E54.middle", {"position": v(90, 20.81) * mm});
            skLineSegment(sketch, "E55.bottom", {"start": v(93, 23.81) * mm, "end": v(87, 23.81) * mm});
            skLineSegment(sketch, "E55.top", {"start": v(93, 17.81) * mm, "end": v(87, 17.81) * mm});
            skLineSegment(sketch, "E55.left", {"start": v(93, 23.81) * mm, "end": v(93, 17.81) * mm});
            skLineSegment(sketch, "E55.right", {"start": v(87, 23.81) * mm, "end": v(87, 17.81) * mm});
            skLineSegment(sketch, "E56.bottom", {"start": v(92, 32) * mm, "end": v(88, 32) * mm});
            skLineSegment(sketch, "E56.top", {"start": v(92, 28) * mm, "end": v(88, 28) * mm});
            skLineSegment(sketch, "E56.left", {"start": v(92, 32) * mm, "end": v(92, 28) * mm});
            skLineSegment(sketch, "E56.right", {"start": v(88, 32) * mm, "end": v(88, 28) * mm});
            skPoint(sketch, "E56.middle", {"position": v(90, 30) * mm});
            skLineSegment(sketch, "E57.bottom", {"start": v(93, 33) * mm, "end": v(87, 33) * mm});
            skLineSegment(sketch, "E57.top", {"start": v(93, 27) * mm, "end": v(87, 27) * mm});
            skLineSegment(sketch, "E57.left", {"start": v(93, 33) * mm, "end": v(93, 27) * mm});
            skLineSegment(sketch, "E57.right", {"start": v(87, 33) * mm, "end": v(87, 27) * mm});
            skLineSegment(sketch, "E58.bottom", {"start": v(92, 42.15) * mm, "end": v(88, 42.15) * mm});
            skLineSegment(sketch, "E58.top", {"start": v(92, 38.15) * mm, "end": v(88, 38.15) * mm});
            skLineSegment(sketch, "E58.left", {"start": v(92, 42.15) * mm, "end": v(92, 38.15) * mm});
            skLineSegment(sketch, "E58.right", {"start": v(88, 42.15) * mm, "end": v(88, 38.15) * mm});
            skPoint(sketch, "E58.middle", {"position": v(90, 40.15) * mm});
            skLineSegment(sketch, "E59.bottom", {"start": v(93, 43.15) * mm, "end": v(87, 43.15) * mm});
            skLineSegment(sketch, "E59.top", {"start": v(93, 37.15) * mm, "end": v(87, 37.15) * mm});
            skLineSegment(sketch, "E59.left", {"start": v(93, 43.15) * mm, "end": v(93, 37.15) * mm});
            skLineSegment(sketch, "E59.right", {"start": v(87, 43.15) * mm, "end": v(87, 37.15) * mm});
            skLineSegment(sketch, "E60.bottom", {"start": v(92.5, 52.15) * mm, "end": v(87.5, 52.15) * mm});
            skLineSegment(sketch, "E60.top", {"start": v(92.5, 48.15) * mm, "end": v(87.5, 48.15) * mm});
            skLineSegment(sketch, "E60.left", {"start": v(92.5, 52.15) * mm, "end": v(92.5, 48.15) * mm});
            skLineSegment(sketch, "E60.right", {"start": v(87.5, 52.15) * mm, "end": v(87.5, 48.15) * mm});
            skPoint(sketch, "E60.middle", {"position": v(90, 50.15) * mm});
            skLineSegment(sketch, "E61.bottom", {"start": v(93, 53.15) * mm, "end": v(87, 53.15) * mm});
            skLineSegment(sketch, "E61.top", {"start": v(93, 47.15) * mm, "end": v(87, 47.15) * mm});
            skLineSegment(sketch, "E61.left", {"start": v(93, 53.15) * mm, "end": v(93, 47.15) * mm});
            skLineSegment(sketch, "E61.right", {"start": v(87, 53.15) * mm, "end": v(87, 47.15) * mm});
            skText(sketch, "E62", { "text": "FDA", "fontName": "OpenSans-Regular.ttf"});
            const initialGuessF0  = {"E19": [0.00942, 0.056, 1, 0, 0.002], "E20": [0.01918, 0.056, 1, 0, 0.002], "E21": [0.02919, 0.056, 1, 0, 0.002], "E22": [0.03913, 0.056, 1, 0, 0.002], "E23": [0.04919, 0.056, 1, 0, 0.002], "E24": [0.05917, 0.056, 1, 0, 0.002], "E25": [0.06918, 0.056, 1, 0, 0.002], "E26": [0.07918, 0.056, 1, 0, 0.002], "E62": [0.08594, 0.056, 1, 0, 0.003]};
            skSetInitialGuess(sketch, initialGuessF0);
            skSolve(sketch);
        }
        {
            var Q0;
            {var subQ0=sQuery(id+"F0.wireOp",EDGE,"E4.1");Q0=makeQuery(id+"F0.imprint","IMPRINT",FACE,{"disambiguationData":[TD([[makeQuery(id+"F0.imprint","IMPRINT",EDGE,{"derivedFrom":subQ0}),-1.0]])]});}
            var Q1;
            Q1=makeQuery(id+"F0.imprint","IMPRINT",FACE,{"disambiguationData":[TD([[makeQuery(id+"F0.imprint","IMPRINT",EDGE,{"derivedFrom":sQuery(id+"F0.wireOp",EDGE,"E0.bottom")}),1.0]])]});
            var Q2;
            Q2=makeQuery(id+"F0.imprint","IMPRINT",FACE,{"disambiguationData":[TD([[makeQuery(id+"F0.imprint","IMPRINT",EDGE,{"derivedFrom":sQuery(id+"F0.wireOp",EDGE,"E3")}),-1.0]])]});
            var Q3;
            Q3=makeQuery(id+"F0.imprint","IMPRINT",FACE,{"disambiguationData":[TD([[makeQuery(id+"F0.imprint","IMPRINT",EDGE,{"derivedFrom":sQuery(id+"F0.wireOp",EDGE,"E5.bottom")}),1.0]])]});
            var Q4;
            {var subQ0=sQuery(id+"F0.wireOp",EDGE,"507ef811-4032-426c-8cf9-381f98ecc6b9.1.0.0");Q4=makeQuery(id+"F0.imprint","IMPRINT",FACE,{"disambiguationData":[TD([[makeQuery(id+"F0.imprint","IMPRINT",EDGE,{"derivedFrom":subQ0}),-1.0]])]});}
            var Q5;
            {var subQ0=sQuery(id+"F0.wireOp",EDGE,"507ef811-4032-426c-8cf9-381f98ecc6b9.2.0.0");Q5=makeQuery(id+"F0.imprint","IMPRINT",FACE,{"disambiguationData":[TD([[makeQuery(id+"F0.imprint","IMPRINT",EDGE,{"derivedFrom":subQ0}),-1.0]])]});}
            var Q6;
            {var subQ1=sQuery(id+"F0.wireOp",EDGE,"507ef811-4032-426c-8cf9-381f98ecc6b9.2.0.0");Q6=makeQuery(id+"F0.imprint","IMPRINT",FACE,{"disambiguationData":[TD([[makeQuery(id+"F0.imprint","IMPRINT",EDGE,{"derivedFrom":subQ1}),1.0]])]});}
            var Q7;
            {var subQ0=sQuery(id+"F0.wireOp",EDGE,"507ef811-4032-426c-8cf9-381f98ecc6b9.3.0.0");Q7=makeQuery(id+"F0.imprint","IMPRINT",FACE,{"disambiguationData":[TD([[makeQuery(id+"F0.imprint","IMPRINT",EDGE,{"derivedFrom":subQ0}),1.0]])]});}
            var Q8;
            {var subQ0=sQuery(id+"F0.wireOp",EDGE,"507ef811-4032-426c-8cf9-381f98ecc6b9.4.0.0");Q8=makeQuery(id+"F0.imprint","IMPRINT",FACE,{"disambiguationData":[TD([[makeQuery(id+"F0.imprint","IMPRINT",EDGE,{"derivedFrom":subQ0}),1.0]])]});}
            var Q9;
            Q9=makeQuery(id+"F0.imprint","IMPRINT",FACE,{"disambiguationData":[TD([[makeQuery(id+"F0.imprint","IMPRINT",EDGE,{"derivedFrom":sQuery(id+"F0.wireOp",EDGE,"E6")}),1.0]])]});
            var Q10;
            Q10=makeQuery(id+"F0.imprint","IMPRINT",FACE,{"disambiguationData":[TD([[makeQuery(id+"F0.imprint","IMPRINT",EDGE,{"derivedFrom":sQuery(id+"F0.wireOp",EDGE,"E7")}),1.0]])]});
            var Q11;
            Q11=makeQuery(id+"F0.imprint","IMPRINT",FACE,{"disambiguationData":[TD([[makeQuery(id+"F0.imprint","IMPRINT",EDGE,{"derivedFrom":sQuery(id+"F0.wireOp",EDGE,"O3tT8Yej-Okk7-LCSe-KlNc-y0QPX2uWYzKY.bottom")}),1.0]])]});
            var Q12;
            Q12=makeQuery(id+"F0.imprint","IMPRINT",FACE,{"disambiguationData":[TD([[makeQuery(id+"F0.imprint","IMPRINT",EDGE,{"derivedFrom":sQuery(id+"F0.wireOp",EDGE,"E3")}),1.0]])]});
            var Q13;
            Q13=makeQuery(id+"F0.imprint","IMPRINT",FACE,{"disambiguationData":[TD([[makeQuery(id+"F0.imprint","IMPRINT",EDGE,{"derivedFrom":sQuery(id+"F0.wireOp",EDGE,"E8.bottom")}),1.0]])]});
            var Q14;
            Q14=makeQuery(id+"F0.imprint","IMPRINT",FACE,{"disambiguationData":[TD([[makeQuery(id+"F0.imprint","IMPRINT",EDGE,{"derivedFrom":sQuery(id+"F0.wireOp",EDGE,"4ae19661-8c38-4b12-a6c4-8219772751d5.1.0.3")}),1.0]])]});
            var Q15;
            {var subQ1=sQuery(id+"F0.wireOp",EDGE,"507ef811-4032-426c-8cf9-381f98ecc6b9.1.0.0");Q15=makeQuery(id+"F0.imprint","IMPRINT",FACE,{"disambiguationData":[TD([[makeQuery(id+"F0.imprint","IMPRINT",EDGE,{"derivedFrom":subQ1}),1.0]])]});}
            var Q16;
            Q16=makeQuery(id+"F0.imprint","IMPRINT",FACE,{"disambiguationData":[TD([[makeQuery(id+"F0.imprint","IMPRINT",EDGE,{"derivedFrom":sQuery(id+"F0.wireOp",EDGE,"4ae19661-8c38-4b12-a6c4-8219772751d5.2.0.3")}),1.0]])]});
            var Q17;
            Q17=makeQuery(id+"F0.imprint","IMPRINT",FACE,{"disambiguationData":[TD([[makeQuery(id+"F0.imprint","IMPRINT",EDGE,{"derivedFrom":sQuery(id+"F0.wireOp",EDGE,"47ba01c2-e299-4726-b962-d3ee39cc78bc.1.0.0")}),1.0]])]});
            var Q18;
            Q18=makeQuery(id+"F0.imprint","IMPRINT",FACE,{"disambiguationData":[TD([[makeQuery(id+"F0.imprint","IMPRINT",EDGE,{"derivedFrom":sQuery(id+"F0.wireOp",EDGE,"4ae19661-8c38-4b12-a6c4-8219772751d5.1.0.1")}),1.0]])]});
            var Q19;
            Q19=makeQuery(id+"F0.imprint","IMPRINT",FACE,{"disambiguationData":[TD([[makeQuery(id+"F0.imprint","IMPRINT",EDGE,{"derivedFrom":sQuery(id+"F0.wireOp",EDGE,"4b779a05-3379-46eb-a5e4-6f14965aae69.1.0.0")}),1.0]])]});
            var Q20;
            Q20=makeQuery(id+"F0.imprint","IMPRINT",FACE,{"disambiguationData":[TD([[makeQuery(id+"F0.imprint","IMPRINT",EDGE,{"derivedFrom":sQuery(id+"F0.wireOp",EDGE,"93a5c984-932f-4202-b3e1-f36a6c73e6e3.1.0.0")}),1.0]])]});
            var Q21;
            Q21=makeQuery(id+"F0.imprint","IMPRINT",FACE,{"disambiguationData":[TD([[makeQuery(id+"F0.imprint","IMPRINT",EDGE,{"derivedFrom":sQuery(id+"F0.wireOp",EDGE,"93a5c984-932f-4202-b3e1-f36a6c73e6e3.2.0.0")}),1.0]])]});
            var Q22;
            Q22=makeQuery(id+"F0.imprint","IMPRINT",FACE,{"disambiguationData":[TD([[makeQuery(id+"F0.imprint","IMPRINT",EDGE,{"derivedFrom":sQuery(id+"F0.wireOp",EDGE,"93a5c984-932f-4202-b3e1-f36a6c73e6e3.3.0.0")}),1.0]])]});
            var Q23;
            Q23=makeQuery(id+"F0.imprint","IMPRINT",FACE,{"disambiguationData":[TD([[makeQuery(id+"F0.imprint","IMPRINT",EDGE,{"derivedFrom":sQuery(id+"F0.wireOp",EDGE,"4b779a05-3379-46eb-a5e4-6f14965aae69.3.0.0")}),1.0]])]});
            var Q24;
            Q24=makeQuery(id+"F0.imprint","IMPRINT",FACE,{"disambiguationData":[TD([[makeQuery(id+"F0.imprint","IMPRINT",EDGE,{"derivedFrom":sQuery(id+"F0.wireOp",EDGE,"4ae19661-8c38-4b12-a6c4-8219772751d5.3.0.1")}),1.0]])]});
            var Q25;
            Q25=makeQuery(id+"F0.imprint","IMPRINT",FACE,{"disambiguationData":[TD([[makeQuery(id+"F0.imprint","IMPRINT",EDGE,{"derivedFrom":sQuery(id+"F0.wireOp",EDGE,"47ba01c2-e299-4726-b962-d3ee39cc78bc.3.0.0")}),1.0]])]});
            var Q26;
            Q26=makeQuery(id+"F0.imprint","IMPRINT",FACE,{"disambiguationData":[TD([[makeQuery(id+"F0.imprint","IMPRINT",EDGE,{"derivedFrom":sQuery(id+"F0.wireOp",EDGE,"47ba01c2-e299-4726-b962-d3ee39cc78bc.2.0.0")}),1.0]])]});
            var Q27;
            Q27=makeQuery(id+"F0.imprint","IMPRINT",FACE,{"disambiguationData":[TD([[makeQuery(id+"F0.imprint","IMPRINT",EDGE,{"derivedFrom":sQuery(id+"F0.wireOp",EDGE,"4ae19661-8c38-4b12-a6c4-8219772751d5.2.0.1")}),1.0]])]});
            var Q28;
            Q28=makeQuery(id+"F0.imprint","IMPRINT",FACE,{"disambiguationData":[TD([[makeQuery(id+"F0.imprint","IMPRINT",EDGE,{"derivedFrom":sQuery(id+"F0.wireOp",EDGE,"4b779a05-3379-46eb-a5e4-6f14965aae69.2.0.0")}),1.0]])]});
            var Q29;
            Q29=makeQuery(id+"F0.imprint","IMPRINT",FACE,{"disambiguationData":[TD([[makeQuery(id+"F0.imprint","IMPRINT",EDGE,{"derivedFrom":sQuery(id+"F0.wireOp",EDGE,"4ae19661-8c38-4b12-a6c4-8219772751d5.3.0.3")}),1.0]])]});
            var Q30;
            Q30=makeQuery(id+"F0.imprint","IMPRINT",FACE,{"disambiguationData":[TD([[makeQuery(id+"F0.imprint","IMPRINT",EDGE,{"derivedFrom":sQuery(id+"F0.wireOp",EDGE,"4b779a05-3379-46eb-a5e4-6f14965aae69.4.0.0")}),1.0]])]});
            var Q31;
            Q31=makeQuery(id+"F0.imprint","IMPRINT",FACE,{"disambiguationData":[TD([[makeQuery(id+"F0.imprint","IMPRINT",EDGE,{"derivedFrom":sQuery(id+"F0.wireOp",EDGE,"4ae19661-8c38-4b12-a6c4-8219772751d5.4.0.1")}),1.0]])]});
            var Q32;
            Q32=makeQuery(id+"F0.imprint","IMPRINT",FACE,{"disambiguationData":[TD([[makeQuery(id+"F0.imprint","IMPRINT",EDGE,{"derivedFrom":sQuery(id+"F0.wireOp",EDGE,"47ba01c2-e299-4726-b962-d3ee39cc78bc.4.0.0")}),1.0]])]});
            var Q33;
            Q33=makeQuery(id+"F0.imprint","IMPRINT",FACE,{"disambiguationData":[TD([[makeQuery(id+"F0.imprint","IMPRINT",EDGE,{"derivedFrom":sQuery(id+"F0.wireOp",EDGE,"4ae19661-8c38-4b12-a6c4-8219772751d5.4.0.3")}),1.0]])]});
            var Q34;
            {var subQ0=sQuery(id+"F0.wireOp",EDGE,"507ef811-4032-426c-8cf9-381f98ecc6b9.5.0.0");Q34=makeQuery(id+"F0.imprint","IMPRINT",FACE,{"disambiguationData":[TD([[makeQuery(id+"F0.imprint","IMPRINT",EDGE,{"derivedFrom":subQ0}),1.0]])]});}
            var Q35;
            Q35=makeQuery(id+"F0.imprint","IMPRINT",FACE,{"disambiguationData":[TD([[makeQuery(id+"F0.imprint","IMPRINT",EDGE,{"derivedFrom":sQuery(id+"F0.wireOp",EDGE,"4ae19661-8c38-4b12-a6c4-8219772751d5.5.0.3")}),1.0]])]});
            var Q36;
            Q36=makeQuery(id+"F0.imprint","IMPRINT",FACE,{"disambiguationData":[TD([[makeQuery(id+"F0.imprint","IMPRINT",EDGE,{"derivedFrom":sQuery(id+"F0.wireOp",EDGE,"47ba01c2-e299-4726-b962-d3ee39cc78bc.5.0.0")}),1.0]])]});
            var Q37;
            Q37=makeQuery(id+"F0.imprint","IMPRINT",FACE,{"disambiguationData":[TD([[makeQuery(id+"F0.imprint","IMPRINT",EDGE,{"derivedFrom":sQuery(id+"F0.wireOp",EDGE,"4ae19661-8c38-4b12-a6c4-8219772751d5.5.0.1")}),1.0]])]});
            var Q38;
            Q38=makeQuery(id+"F0.imprint","IMPRINT",FACE,{"disambiguationData":[TD([[makeQuery(id+"F0.imprint","IMPRINT",EDGE,{"derivedFrom":sQuery(id+"F0.wireOp",EDGE,"93a5c984-932f-4202-b3e1-f36a6c73e6e3.4.0.0")}),1.0]])]});
            var Q39;
            Q39=makeQuery(id+"F0.imprint","IMPRINT",FACE,{"disambiguationData":[TD([[makeQuery(id+"F0.imprint","IMPRINT",EDGE,{"derivedFrom":sQuery(id+"F0.wireOp",EDGE,"93a5c984-932f-4202-b3e1-f36a6c73e6e3.5.0.0")}),1.0]])]});
            var Q40;
            {var subQ0=sQuery(id+"F0.wireOp",EDGE,"507ef811-4032-426c-8cf9-381f98ecc6b9.5.0.0");Q40=makeQuery(id+"F0.imprint","IMPRINT",FACE,{"disambiguationData":[TD([[makeQuery(id+"F0.imprint","IMPRINT",EDGE,{"derivedFrom":subQ0}),-1.0]])]});}
            var Q41;
            {var subQ0=sQuery(id+"F0.wireOp",EDGE,"507ef811-4032-426c-8cf9-381f98ecc6b9.4.0.0");Q41=makeQuery(id+"F0.imprint","IMPRINT",FACE,{"disambiguationData":[TD([[makeQuery(id+"F0.imprint","IMPRINT",EDGE,{"derivedFrom":subQ0}),-1.0]])]});}
            var Q42;
            {var subQ0=sQuery(id+"F0.wireOp",EDGE,"507ef811-4032-426c-8cf9-381f98ecc6b9.3.0.0");Q42=makeQuery(id+"F0.imprint","IMPRINT",FACE,{"disambiguationData":[TD([[makeQuery(id+"F0.imprint","IMPRINT",EDGE,{"derivedFrom":subQ0}),-1.0]])]});}
            var Q43;
            Q43=makeQuery(id+"F0.imprint","IMPRINT",FACE,{"disambiguationData":[TD([[makeQuery(id+"F0.imprint","IMPRINT",EDGE,{"derivedFrom":sQuery(id+"F0.wireOp",EDGE,"93a5c984-932f-4202-b3e1-f36a6c73e6e3.6.0.0")}),1.0]])]});
            var Q44;
            {var subQ0=sQuery(id+"F0.wireOp",EDGE,"507ef811-4032-426c-8cf9-381f98ecc6b9.6.0.0");Q44=makeQuery(id+"F0.imprint","IMPRINT",FACE,{"disambiguationData":[TD([[makeQuery(id+"F0.imprint","IMPRINT",EDGE,{"derivedFrom":subQ0}),-1.0]])]});}
            var Q45;
            Q45=makeQuery(id+"F0.imprint","IMPRINT",FACE,{"disambiguationData":[TD([[makeQuery(id+"F0.imprint","IMPRINT",EDGE,{"derivedFrom":sQuery(id+"F0.wireOp",EDGE,"93a5c984-932f-4202-b3e1-f36a6c73e6e3.7.0.0")}),1.0]])]});
            var Q46;
            Q46=makeQuery(id+"F0.imprint","IMPRINT",FACE,{"disambiguationData":[TD([[makeQuery(id+"F0.imprint","IMPRINT",EDGE,{"derivedFrom":sQuery(id+"F0.wireOp",EDGE,"4b779a05-3379-46eb-a5e4-6f14965aae69.6.0.0")}),1.0]])]});
            var Q47;
            {var subQ0=sQuery(id+"F0.wireOp",EDGE,"507ef811-4032-426c-8cf9-381f98ecc6b9.6.0.0");Q47=makeQuery(id+"F0.imprint","IMPRINT",FACE,{"disambiguationData":[TD([[makeQuery(id+"F0.imprint","IMPRINT",EDGE,{"derivedFrom":subQ0}),1.0]])]});}
            var Q48;
            Q48=makeQuery(id+"F0.imprint","IMPRINT",FACE,{"disambiguationData":[TD([[makeQuery(id+"F0.imprint","IMPRINT",EDGE,{"derivedFrom":sQuery(id+"F0.wireOp",EDGE,"4ae19661-8c38-4b12-a6c4-8219772751d5.6.0.1")}),1.0]])]});
            var Q49;
            Q49=makeQuery(id+"F0.imprint","IMPRINT",FACE,{"disambiguationData":[TD([[makeQuery(id+"F0.imprint","IMPRINT",EDGE,{"derivedFrom":sQuery(id+"F0.wireOp",EDGE,"4b779a05-3379-46eb-a5e4-6f14965aae69.7.0.0")}),1.0]])]});
            var Q50;
            {var subQ1=sQuery(id+"F0.wireOp",EDGE,"507ef811-4032-426c-8cf9-381f98ecc6b9.7.0.0");Q50=makeQuery(id+"F0.imprint","IMPRINT",FACE,{"disambiguationData":[TD([[makeQuery(id+"F0.imprint","IMPRINT",EDGE,{"derivedFrom":subQ1}),1.0]])]});}
            var Q51;
            {var subQ0=sQuery(id+"F0.wireOp",EDGE,"E4.3");Q51=makeQuery(id+"F0.imprint","IMPRINT",FACE,{"disambiguationData":[TD([[makeQuery(id+"F0.imprint","IMPRINT",EDGE,{"derivedFrom":subQ0}),1.0]])]});}
            var Q52;
            Q52=makeQuery(id+"F0.imprint","IMPRINT",FACE,{"disambiguationData":[TD([[makeQuery(id+"F0.imprint","IMPRINT",EDGE,{"derivedFrom":sQuery(id+"F0.wireOp",EDGE,"47ba01c2-e299-4726-b962-d3ee39cc78bc.7.0.0")}),1.0]])]});
            var Q53;
            Q53=makeQuery(id+"F0.imprint","IMPRINT",FACE,{"disambiguationData":[TD([[makeQuery(id+"F0.imprint","IMPRINT",EDGE,{"derivedFrom":sQuery(id+"F0.wireOp",EDGE,"4ae19661-8c38-4b12-a6c4-8219772751d5.7.0.3")}),1.0]])]});
            var Q54;
            Q54=makeQuery(id+"F0.imprint","IMPRINT",FACE,{"disambiguationData":[TD([[makeQuery(id+"F0.imprint","IMPRINT",EDGE,{"derivedFrom":sQuery(id+"F0.wireOp",EDGE,"4ae19661-8c38-4b12-a6c4-8219772751d5.6.0.3")}),1.0]])]});
            var Q55;
            Q55=makeQuery(id+"F0.imprint","IMPRINT",FACE,{"disambiguationData":[TD([[makeQuery(id+"F0.imprint","IMPRINT",EDGE,{"derivedFrom":sQuery(id+"F0.wireOp",EDGE,"4ae19661-8c38-4b12-a6c4-8219772751d5.7.0.1")}),1.0]])]});
            var Q56;
            {var subQ0=sQuery(id+"F0.wireOp",EDGE,"507ef811-4032-426c-8cf9-381f98ecc6b9.8.0.0");Q56=makeQuery(id+"F0.imprint","IMPRINT",FACE,{"disambiguationData":[TD([[makeQuery(id+"F0.imprint","IMPRINT",EDGE,{"derivedFrom":subQ0}),-1.0]])]});}
            var Q57;
            {var subQ0=sQuery(id+"F0.wireOp",EDGE,"507ef811-4032-426c-8cf9-381f98ecc6b9.7.0.0");Q57=makeQuery(id+"F0.imprint","IMPRINT",FACE,{"disambiguationData":[TD([[makeQuery(id+"F0.imprint","IMPRINT",EDGE,{"derivedFrom":subQ0}),-1.0]])]});}
            var Q58;
            Q58=makeQuery(id+"F0.imprint","IMPRINT",FACE,{"disambiguationData":[TD([[makeQuery(id+"F0.imprint","IMPRINT",EDGE,{"derivedFrom":sQuery(id+"F0.wireOp",EDGE,"47ba01c2-e299-4726-b962-d3ee39cc78bc.6.0.0")}),1.0]])]});
            var Q59;
            Q59=makeQuery(id+"F0.imprint","IMPRINT",FACE,{"disambiguationData":[TD([[makeQuery(id+"F0.imprint","IMPRINT",EDGE,{"derivedFrom":sQuery(id+"F0.wireOp",EDGE,"4b779a05-3379-46eb-a5e4-6f14965aae69.5.0.0")}),1.0]])]});
            var Q60;
            {var subQ0=sQuery(id+"F0.wireOp",EDGE,"E17.1.0.2");Q60=makeQuery(id+"F0.imprint","IMPRINT",FACE,{"disambiguationData":[TD([[makeQuery(id+"F0.imprint","IMPRINT",EDGE,{"derivedFrom":subQ0}),1.0]])]});}
            var Q61;
            {var subQ0=sQuery(id+"F0.wireOp",EDGE,"E17.2.0.2");Q61=makeQuery(id+"F0.imprint","IMPRINT",FACE,{"disambiguationData":[TD([[makeQuery(id+"F0.imprint","IMPRINT",EDGE,{"derivedFrom":subQ0}),1.0]])]});}
            var Q62;
            {var subQ1=sQuery(id+"F0.wireOp",EDGE,"E17.3.0.2");Q62=makeQuery(id+"F0.imprint","IMPRINT",FACE,{"disambiguationData":[TD([[makeQuery(id+"F0.imprint","IMPRINT",EDGE,{"derivedFrom":subQ1}),1.0]])]});}
            var Q63;
            {var subQ0=sQuery(id+"F0.wireOp",EDGE,"E17.4.0.2");Q63=makeQuery(id+"F0.imprint","IMPRINT",FACE,{"disambiguationData":[TD([[makeQuery(id+"F0.imprint","IMPRINT",EDGE,{"derivedFrom":subQ0}),1.0]])]});}
            var Q64;
            {var subQ0=sQuery(id+"F0.wireOp",EDGE,"E17.5.0.2");Q64=makeQuery(id+"F0.imprint","IMPRINT",FACE,{"disambiguationData":[TD([[makeQuery(id+"F0.imprint","IMPRINT",EDGE,{"derivedFrom":subQ0}),1.0]])]});}
            var Q65;
            {var subQ1=sQuery(id+"F0.wireOp",EDGE,"E17.6.0.2");Q65=makeQuery(id+"F0.imprint","IMPRINT",FACE,{"disambiguationData":[TD([[makeQuery(id+"F0.imprint","IMPRINT",EDGE,{"derivedFrom":subQ1}),1.0]])]});}
            var Q66;
            {var subQ0=sQuery(id+"F0.wireOp",EDGE,"E17.7.0.2");Q66=makeQuery(id+"F0.imprint","IMPRINT",FACE,{"disambiguationData":[TD([[makeQuery(id+"F0.imprint","IMPRINT",EDGE,{"derivedFrom":subQ0}),1.0]])]});}
            var Q67;
            Q67=makeQuery(id+"F0.imprint","IMPRINT",FACE,{"disambiguationData":[TD([[makeQuery(id+"F0.imprint","IMPRINT",EDGE,{"derivedFrom":sQuery(id+"F0.wireOp",EDGE,"E15.bottom")}),-1.0]])]});
            var Q68;
            Q68=makeQuery(id+"F0.imprint","IMPRINT",FACE,{"disambiguationData":[TD([[makeQuery(id+"F0.imprint","IMPRINT",EDGE,{"derivedFrom":sQuery(id+"F0.wireOp",EDGE,"E18.1.0.2")}),1.0]])]});
            var Q69;
            Q69=makeQuery(id+"F0.imprint","IMPRINT",FACE,{"disambiguationData":[TD([[makeQuery(id+"F0.imprint","IMPRINT",EDGE,{"derivedFrom":sQuery(id+"F0.wireOp",EDGE,"E18.1.0.6")}),1.0]])]});
            var Q70;
            Q70=makeQuery(id+"F0.imprint","IMPRINT",FACE,{"disambiguationData":[TD([[makeQuery(id+"F0.imprint","IMPRINT",EDGE,{"derivedFrom":sQuery(id+"F0.wireOp",EDGE,"E18.1.0.16")}),-1.0]])]});
            var Q71;
            Q71=makeQuery(id+"F0.imprint","IMPRINT",FACE,{"disambiguationData":[TD([[makeQuery(id+"F0.imprint","IMPRINT",EDGE,{"derivedFrom":sQuery(id+"F0.wireOp",EDGE,"E18.2.0.12")}),-1.0]])]});
            var Q72;
            Q72=makeQuery(id+"F0.imprint","IMPRINT",FACE,{"disambiguationData":[TD([[makeQuery(id+"F0.imprint","IMPRINT",EDGE,{"derivedFrom":sQuery(id+"F0.wireOp",EDGE,"E18.3.0.12")}),-1.0]])]});
            var Q73;
            Q73=makeQuery(id+"F0.imprint","IMPRINT",FACE,{"disambiguationData":[TD([[makeQuery(id+"F0.imprint","IMPRINT",EDGE,{"derivedFrom":sQuery(id+"F0.wireOp",EDGE,"E18.1.0.12")}),-1.0]])]});
            var Q74;
            Q74=makeQuery(id+"F0.imprint","IMPRINT",FACE,{"disambiguationData":[TD([[makeQuery(id+"F0.imprint","IMPRINT",EDGE,{"derivedFrom":sQuery(id+"F0.wireOp",EDGE,"E18.4.0.12")}),-1.0]])]});
            var Q75;
            Q75=makeQuery(id+"F0.imprint","IMPRINT",FACE,{"disambiguationData":[TD([[makeQuery(id+"F0.imprint","IMPRINT",EDGE,{"derivedFrom":sQuery(id+"F0.wireOp",EDGE,"E18.6.0.12")}),-1.0]])]});
            var Q76;
            Q76=makeQuery(id+"F0.imprint","IMPRINT",FACE,{"disambiguationData":[TD([[makeQuery(id+"F0.imprint","IMPRINT",EDGE,{"derivedFrom":sQuery(id+"F0.wireOp",EDGE,"E18.5.0.12")}),-1.0]])]});
            var Q77;
            Q77=makeQuery(id+"F0.imprint","IMPRINT",FACE,{"disambiguationData":[TD([[makeQuery(id+"F0.imprint","IMPRINT",EDGE,{"derivedFrom":sQuery(id+"F0.wireOp",EDGE,"E18.5.0.16")}),-1.0]])]});
            var Q78;
            Q78=makeQuery(id+"F0.imprint","IMPRINT",FACE,{"disambiguationData":[TD([[makeQuery(id+"F0.imprint","IMPRINT",EDGE,{"derivedFrom":sQuery(id+"F0.wireOp",EDGE,"E18.4.0.16")}),-1.0]])]});
            var Q79;
            Q79=makeQuery(id+"F0.imprint","IMPRINT",FACE,{"disambiguationData":[TD([[makeQuery(id+"F0.imprint","IMPRINT",EDGE,{"derivedFrom":sQuery(id+"F0.wireOp",EDGE,"E18.3.0.16")}),-1.0]])]});
            var Q80;
            Q80=makeQuery(id+"F0.imprint","IMPRINT",FACE,{"disambiguationData":[TD([[makeQuery(id+"F0.imprint","IMPRINT",EDGE,{"derivedFrom":sQuery(id+"F0.wireOp",EDGE,"E18.2.0.16")}),-1.0]])]});
            var Q81;
            Q81=makeQuery(id+"F0.imprint","IMPRINT",FACE,{"disambiguationData":[TD([[makeQuery(id+"F0.imprint","IMPRINT",EDGE,{"derivedFrom":sQuery(id+"F0.wireOp",EDGE,"E18.7.0.12")}),-1.0]])]});
            var Q82;
            Q82=makeQuery(id+"F0.imprint","IMPRINT",FACE,{"disambiguationData":[TD([[makeQuery(id+"F0.imprint","IMPRINT",EDGE,{"derivedFrom":sQuery(id+"F0.wireOp",EDGE,"E18.6.0.16")}),-1.0]])]});
            var Q83;
            Q83=makeQuery(id+"F0.imprint","IMPRINT",FACE,{"disambiguationData":[TD([[makeQuery(id+"F0.imprint","IMPRINT",EDGE,{"derivedFrom":sQuery(id+"F0.wireOp",EDGE,"E18.7.0.16")}),-1.0]])]});
            var Q84;
            Q84=makeQuery(id+"F0.imprint","IMPRINT",FACE,{"disambiguationData":[TD([[makeQuery(id+"F0.imprint","IMPRINT",EDGE,{"derivedFrom":sQuery(id+"F0.wireOp",EDGE,"E18.7.0.6")}),1.0]])]});
            var Q85;
            Q85=makeQuery(id+"F0.imprint","IMPRINT",FACE,{"disambiguationData":[TD([[makeQuery(id+"F0.imprint","IMPRINT",EDGE,{"derivedFrom":sQuery(id+"F0.wireOp",EDGE,"E18.6.0.6")}),1.0]])]});
            var Q86;
            Q86=makeQuery(id+"F0.imprint","IMPRINT",FACE,{"disambiguationData":[TD([[makeQuery(id+"F0.imprint","IMPRINT",EDGE,{"derivedFrom":sQuery(id+"F0.wireOp",EDGE,"E18.5.0.6")}),1.0]])]});
            var Q87;
            Q87=makeQuery(id+"F0.imprint","IMPRINT",FACE,{"disambiguationData":[TD([[makeQuery(id+"F0.imprint","IMPRINT",EDGE,{"derivedFrom":sQuery(id+"F0.wireOp",EDGE,"E18.4.0.6")}),1.0]])]});
            var Q88;
            Q88=makeQuery(id+"F0.imprint","IMPRINT",FACE,{"disambiguationData":[TD([[makeQuery(id+"F0.imprint","IMPRINT",EDGE,{"derivedFrom":sQuery(id+"F0.wireOp",EDGE,"E18.4.0.2")}),1.0]])]});
            var Q89;
            Q89=makeQuery(id+"F0.imprint","IMPRINT",FACE,{"disambiguationData":[TD([[makeQuery(id+"F0.imprint","IMPRINT",EDGE,{"derivedFrom":sQuery(id+"F0.wireOp",EDGE,"E18.5.0.2")}),1.0]])]});
            var Q90;
            Q90=makeQuery(id+"F0.imprint","IMPRINT",FACE,{"disambiguationData":[TD([[makeQuery(id+"F0.imprint","IMPRINT",EDGE,{"derivedFrom":sQuery(id+"F0.wireOp",EDGE,"E18.6.0.2")}),1.0]])]});
            var Q91;
            Q91=makeQuery(id+"F0.imprint","IMPRINT",FACE,{"disambiguationData":[TD([[makeQuery(id+"F0.imprint","IMPRINT",EDGE,{"derivedFrom":sQuery(id+"F0.wireOp",EDGE,"E18.7.0.2")}),1.0]])]});
            var Q92;
            Q92=makeQuery(id+"F0.imprint","IMPRINT",FACE,{"disambiguationData":[TD([[makeQuery(id+"F0.imprint","IMPRINT",EDGE,{"derivedFrom":sQuery(id+"F0.wireOp",EDGE,"E18.3.0.2")}),1.0]])]});
            var Q93;
            Q93=makeQuery(id+"F0.imprint","IMPRINT",FACE,{"disambiguationData":[TD([[makeQuery(id+"F0.imprint","IMPRINT",EDGE,{"derivedFrom":sQuery(id+"F0.wireOp",EDGE,"E18.2.0.6")}),1.0]])]});
            var Q94;
            Q94=makeQuery(id+"F0.imprint","IMPRINT",FACE,{"disambiguationData":[TD([[makeQuery(id+"F0.imprint","IMPRINT",EDGE,{"derivedFrom":sQuery(id+"F0.wireOp",EDGE,"E18.3.0.6")}),1.0]])]});
            var Q95;
            Q95=makeQuery(id+"F0.imprint","IMPRINT",FACE,{"disambiguationData":[TD([[makeQuery(id+"F0.imprint","IMPRINT",EDGE,{"derivedFrom":sQuery(id+"F0.wireOp",EDGE,"E18.2.0.2")}),1.0]])]});
            var Q96;
            Q96=makeQuery(id+"F0.imprint","IMPRINT",FACE,{"disambiguationData":[TD([[makeQuery(id+"F0.imprint","IMPRINT",EDGE,{"derivedFrom":sQuery(id+"F0.wireOp",EDGE,"E18.1.0.0")}),1.0]])]});
            var Q97;
            Q97=makeQuery(id+"F0.imprint","IMPRINT",FACE,{"disambiguationData":[TD([[makeQuery(id+"F0.imprint","IMPRINT",EDGE,{"derivedFrom":sQuery(id+"F0.wireOp",EDGE,"E18.2.0.0")}),1.0]])]});
            var Q98;
            Q98=makeQuery(id+"F0.imprint","IMPRINT",FACE,{"disambiguationData":[TD([[makeQuery(id+"F0.imprint","IMPRINT",EDGE,{"derivedFrom":sQuery(id+"F0.wireOp",EDGE,"E18.3.0.0")}),1.0]])]});
            var Q99;
            Q99=makeQuery(id+"F0.imprint","IMPRINT",FACE,{"disambiguationData":[TD([[makeQuery(id+"F0.imprint","IMPRINT",EDGE,{"derivedFrom":sQuery(id+"F0.wireOp",EDGE,"E18.4.0.0")}),1.0]])]});
            var Q100;
            Q100=makeQuery(id+"F0.imprint","IMPRINT",FACE,{"disambiguationData":[TD([[makeQuery(id+"F0.imprint","IMPRINT",EDGE,{"derivedFrom":sQuery(id+"F0.wireOp",EDGE,"E18.5.0.0")}),1.0]])]});
            var Q101;
            Q101=makeQuery(id+"F0.imprint","IMPRINT",FACE,{"disambiguationData":[TD([[makeQuery(id+"F0.imprint","IMPRINT",EDGE,{"derivedFrom":sQuery(id+"F0.wireOp",EDGE,"E18.6.0.0")}),1.0]])]});
            var Q102;
            Q102=makeQuery(id+"F0.imprint","IMPRINT",FACE,{"disambiguationData":[TD([[makeQuery(id+"F0.imprint","IMPRINT",EDGE,{"derivedFrom":sQuery(id+"F0.wireOp",EDGE,"E18.7.0.0")}),1.0]])]});
            var Q103;
            {var subQ0=sQuery(id+"F0.wireOp",EDGE,"E17.1.0.0");Q103=makeQuery(id+"F0.imprint","IMPRINT",FACE,{"disambiguationData":[TD([[makeQuery(id+"F0.imprint","IMPRINT",EDGE,{"derivedFrom":subQ0}),1.0]])]});}
            var Q104;
            {var subQ0=sQuery(id+"F0.wireOp",EDGE,"E17.2.0.0");Q104=makeQuery(id+"F0.imprint","IMPRINT",FACE,{"disambiguationData":[TD([[makeQuery(id+"F0.imprint","IMPRINT",EDGE,{"derivedFrom":subQ0}),1.0]])]});}
            var Q105;
            {var subQ0=sQuery(id+"F0.wireOp",EDGE,"E17.3.0.0");Q105=makeQuery(id+"F0.imprint","IMPRINT",FACE,{"disambiguationData":[TD([[makeQuery(id+"F0.imprint","IMPRINT",EDGE,{"derivedFrom":subQ0}),1.0]])]});}
            var Q106;
            {var subQ0=sQuery(id+"F0.wireOp",EDGE,"E17.4.0.0");Q106=makeQuery(id+"F0.imprint","IMPRINT",FACE,{"disambiguationData":[TD([[makeQuery(id+"F0.imprint","IMPRINT",EDGE,{"derivedFrom":subQ0}),1.0]])]});}
            var Q107;
            {var subQ0=sQuery(id+"F0.wireOp",EDGE,"E17.5.0.0");Q107=makeQuery(id+"F0.imprint","IMPRINT",FACE,{"disambiguationData":[TD([[makeQuery(id+"F0.imprint","IMPRINT",EDGE,{"derivedFrom":subQ0}),1.0]])]});}
            var Q108;
            {var subQ0=sQuery(id+"F0.wireOp",EDGE,"E17.6.0.0");Q108=makeQuery(id+"F0.imprint","IMPRINT",FACE,{"disambiguationData":[TD([[makeQuery(id+"F0.imprint","IMPRINT",EDGE,{"derivedFrom":subQ0}),1.0]])]});}
            var Q109;
            {var subQ0=sQuery(id+"F0.wireOp",EDGE,"E17.7.0.0");Q109=makeQuery(id+"F0.imprint","IMPRINT",FACE,{"disambiguationData":[TD([[makeQuery(id+"F0.imprint","IMPRINT",EDGE,{"derivedFrom":subQ0}),1.0]])]});}
            var Q110;
            {var subQ0=sQuery(id+"F0.wireOp",EDGE,"E17.8.0.0");Q110=makeQuery(id+"F0.imprint","IMPRINT",FACE,{"disambiguationData":[TD([[makeQuery(id+"F0.imprint","IMPRINT",EDGE,{"derivedFrom":subQ0}),1.0]])]});}
            var Q111;
            Q111=makeQuery(id+"F0.imprint","IMPRINT",FACE,{"disambiguationData":[TD([[makeQuery(id+"F0.imprint","IMPRINT",EDGE,{"derivedFrom":sQuery(id+"F0.wireOp",EDGE,"E19.sketch_text.stroke-0")}),-1.0]])]});
            var Q112;
            Q112=makeQuery(id+"F0.imprint","IMPRINT",FACE,{"disambiguationData":[TD([[makeQuery(id+"F0.imprint","IMPRINT",EDGE,{"derivedFrom":sQuery(id+"F0.wireOp",EDGE,"E60.bottom")}),-1.0]])]});
            var Q113;
            Q113=makeQuery(id+"F0.imprint","IMPRINT",FACE,{"disambiguationData":[TD([[makeQuery(id+"F0.imprint","IMPRINT",EDGE,{"derivedFrom":sQuery(id+"F0.wireOp",EDGE,"E58.bottom")}),-1.0]])]});
            var Q114;
            Q114=makeQuery(id+"F0.imprint","IMPRINT",FACE,{"disambiguationData":[TD([[makeQuery(id+"F0.imprint","IMPRINT",EDGE,{"derivedFrom":sQuery(id+"F0.wireOp",EDGE,"E56.bottom")}),-1.0]])]});
            var Q115;
            Q115=makeQuery(id+"F0.imprint","IMPRINT",FACE,{"disambiguationData":[TD([[makeQuery(id+"F0.imprint","IMPRINT",EDGE,{"derivedFrom":sQuery(id+"F0.wireOp",EDGE,"E54.bottom")}),-1.0]])]});
            var Q116;
            Q116=makeQuery(id+"F0.imprint","IMPRINT",FACE,{"disambiguationData":[TD([[makeQuery(id+"F0.imprint","IMPRINT",EDGE,{"derivedFrom":sQuery(id+"F0.wireOp",EDGE,"E52.bottom")}),-1.0]])]});
            var Q117;
            Q117=makeQuery(id+"F0.imprint","IMPRINT",FACE,{"disambiguationData":[TD([[makeQuery(id+"F0.imprint","IMPRINT",EDGE,{"derivedFrom":sQuery(id+"F0.wireOp",EDGE,"E20.sketch_text.stroke-0")}),-1.0]])]});
            var Q118;
            Q118=makeQuery(id+"F0.imprint","IMPRINT",FACE,{"disambiguationData":[TD([[makeQuery(id+"F0.imprint","IMPRINT",EDGE,{"derivedFrom":sQuery(id+"F0.wireOp",EDGE,"E21.sketch_text.stroke-0")}),-1.0]])]});
            var Q119;
            Q119=makeQuery(id+"F0.imprint","IMPRINT",FACE,{"disambiguationData":[TD([[makeQuery(id+"F0.imprint","IMPRINT",EDGE,{"derivedFrom":sQuery(id+"F0.wireOp",EDGE,"E22.sketch_text.stroke-0")}),-1.0]])]});
            var Q120;
            Q120=makeQuery(id+"F0.imprint","IMPRINT",FACE,{"disambiguationData":[TD([[makeQuery(id+"F0.imprint","IMPRINT",EDGE,{"derivedFrom":sQuery(id+"F0.wireOp",EDGE,"E22.sketch_text.stroke-11")}),1.0]])]});
            var Q121;
            Q121=makeQuery(id+"F0.imprint","IMPRINT",FACE,{"disambiguationData":[TD([[makeQuery(id+"F0.imprint","IMPRINT",EDGE,{"derivedFrom":sQuery(id+"F0.wireOp",EDGE,"E24.sketch_text.stroke-15")}),1.0]])]});
            var Q122;
            Q122=makeQuery(id+"F0.imprint","IMPRINT",FACE,{"disambiguationData":[TD([[makeQuery(id+"F0.imprint","IMPRINT",EDGE,{"derivedFrom":sQuery(id+"F0.wireOp",EDGE,"E24.sketch_text.stroke-0")}),-1.0]])]});
            var Q123;
            {var subQ0=sQuery(id+"F0.wireOp",EDGE,"E24.sketch_text.stroke-13");var subQ1=sQuery(id+"F0.wireOp",EDGE,"E4.0");var subQ2=makeQuery(id+"F0.imprint","INTERSECT",VERTEX,{"derivedFrom":[subQ1,subQ0]});Q123=makeQuery(id+"F0.imprint","IMPRINT",FACE,{"disambiguationData":[TD([[makeQuery(id+"F0.imprint","IMPRINT",EDGE,{"disambiguationData":[TD([[subQ2,-1.0]])],"derivedFrom":subQ1}),-1.0]])]});}
            var Q124;
            {var subQ5=sQuery(id+"F0.wireOp",EDGE,"E21.sketch_text.stroke-7");Q124=makeQuery(id+"F0.imprint","IMPRINT",FACE,{"disambiguationData":[TD([[makeQuery(id+"F0.imprint","IMPRINT",EDGE,{"derivedFrom":subQ5}),-1.0]])]});}
            var Q125;
            Q125=makeQuery(id+"F0.imprint","IMPRINT",FACE,{"disambiguationData":[TD([[makeQuery(id+"F0.imprint","IMPRINT",EDGE,{"derivedFrom":sQuery(id+"F0.wireOp",EDGE,"E26.sketch_text.stroke-0")}),-1.0]])]});
            var Q126;
            {var subQ0=sQuery(id+"F0.wireOp",EDGE,"E26.sketch_text.stroke-8");var subQ1=sQuery(id+"F0.wireOp",EDGE,"E4.0");var subQ2=makeQuery(id+"F0.imprint","INTERSECT",VERTEX,{"derivedFrom":[subQ1,subQ0]});Q126=makeQuery(id+"F0.imprint","IMPRINT",FACE,{"disambiguationData":[TD([[makeQuery(id+"F0.imprint","IMPRINT",EDGE,{"disambiguationData":[TD([[subQ2,-1.0]])],"derivedFrom":subQ1}),-1.0]])]});}
            var Q127;
            Q127=makeQuery(id+"F0.imprint","IMPRINT",FACE,{"disambiguationData":[TD([[makeQuery(id+"F0.imprint","IMPRINT",EDGE,{"derivedFrom":sQuery(id+"F0.wireOp",EDGE,"E26.sketch_text.stroke-15")}),1.0]])]});
            var Q128;
            Q128=makeQuery(id+"F0.imprint","IMPRINT",FACE,{"disambiguationData":[TD([[makeQuery(id+"F0.imprint","IMPRINT",EDGE,{"derivedFrom":sQuery(id+"F0.wireOp",EDGE,"E26.sketch_text.stroke-23")}),1.0]])]});
            var Q129;
            Q129=makeQuery(id+"F0.imprint","IMPRINT",FACE,{"disambiguationData":[TD([[makeQuery(id+"F0.imprint","IMPRINT",EDGE,{"derivedFrom":sQuery(id+"F0.wireOp",EDGE,"E25.sketch_text.stroke-0")}),-1.0]])]});
            var Q130;
            Q130=makeQuery(id+"F0.imprint","IMPRINT",FACE,{"disambiguationData":[TD([[makeQuery(id+"F0.imprint","IMPRINT",EDGE,{"derivedFrom":sQuery(id+"F0.wireOp",EDGE,"E23.sketch_text.stroke-0")}),-1.0]])]});
            var Q131;
            {var subQ0=sQuery(id+"F0.wireOp",EDGE,"E23.sketch_text.stroke-4");var subQ1=sQuery(id+"F0.wireOp",EDGE,"E4.0");var subQ2=makeQuery(id+"F0.imprint","INTERSECT",VERTEX,{"derivedFrom":[subQ1,subQ0]});Q131=makeQuery(id+"F0.imprint","IMPRINT",FACE,{"disambiguationData":[TD([[makeQuery(id+"F0.imprint","IMPRINT",EDGE,{"disambiguationData":[TD([[subQ2,-1.0]])],"derivedFrom":subQ1}),-1.0]])]});}
            var Q132;
            Q132=makeQuery(id+"F0.imprint","IMPRINT",FACE,{"disambiguationData":[TD([[makeQuery(id+"F0.imprint","IMPRINT",EDGE,{"derivedFrom":sQuery(id+"F0.wireOp",EDGE,"E62.sketch_text.stroke-0")}),-1.0]])]});
            var Q133;
            Q133=makeQuery(id+"F0.imprint","IMPRINT",FACE,{"disambiguationData":[TD([[makeQuery(id+"F0.imprint","IMPRINT",EDGE,{"derivedFrom":sQuery(id+"F0.wireOp",EDGE,"E62.sketch_text.stroke-10")}),-1.0]])]});
            var Q134;
            Q134=makeQuery(id+"F0.imprint","IMPRINT",FACE,{"disambiguationData":[TD([[makeQuery(id+"F0.imprint","IMPRINT",EDGE,{"derivedFrom":sQuery(id+"F0.wireOp",EDGE,"E62.sketch_text.stroke-17")}),1.0]])]});
            var Q135;
            {var subQ0=sQuery(id+"F0.wireOp",EDGE,"E62.sketch_text.stroke-24");Q135=makeQuery(id+"F0.imprint","IMPRINT",FACE,{"disambiguationData":[TD([[makeQuery(id+"F0.imprint","IMPRINT",EDGE,{"derivedFrom":subQ0}),1.0]])]});}
            var Q136;
            Q136=makeQuery(id+"F0.imprint","IMPRINT",FACE,{"disambiguationData":[TD([[makeQuery(id+"F0.imprint","IMPRINT",EDGE,{"derivedFrom":sQuery(id+"F0.wireOp",EDGE,"E62.sketch_text.stroke-24")}),-1.0]])]});
            var Q137;
            Q137=makeQuery(id+"F0.imprint","IMPRINT",FACE,{"disambiguationData":[TD([[makeQuery(id+"F0.imprint","IMPRINT",EDGE,{"derivedFrom":sQuery(id+"F0.wireOp",EDGE,"E62.sketch_text.stroke-32")}),1.0]])]});
            extrude(context, id + "F1", {"entities" : qUnion([Q0, Q1, Q2, Q3, Q4, Q5, Q6, Q7, Q8, Q9, Q10, Q11, Q12, Q13, Q14, Q15, Q16, Q17, Q18, Q19, Q20, Q21, Q22, Q23, Q24, Q25, Q26, Q27, Q28, Q29, Q30, Q31, Q32, Q33, Q34, Q35, Q36, Q37, Q38, Q39, Q40, Q41, Q42, Q43, Q44, Q45, Q46, Q47, Q48, Q49, Q50, Q51, Q52, Q53, Q54, Q55, Q56, Q57, Q58, Q59, Q60, Q61, Q62, Q63, Q64, Q65, Q66, Q67, Q68, Q69, Q70, Q71, Q72, Q73, Q74, Q75, Q76, Q77, Q78, Q79, Q80, Q81, Q82, Q83, Q84, Q85, Q86, Q87, Q88, Q89, Q90, Q91, Q92, Q93, Q94, Q95, Q96, Q97, Q98, Q99, Q100, Q101, Q102, Q103, Q104, Q105, Q106, Q107, Q108, Q109, Q110, Q111, Q112, Q113, Q114, Q115, Q116, Q117, Q118, Q119, Q120, Q121, Q122, Q123, Q124, Q125, Q126, Q127, Q128, Q129, Q130, Q131, Q132, Q133, Q134, Q135, Q136, Q137]), "oppositeDirection" : true, "depth" : 10 * mm});
        }
        {
            var Q0;
            Q0=makeQuery(id+"F1.opExtrude","CAP_FACE",FACE,{"disambiguationData":[OSD([sQuery(id+"F0.wireOp",EDGE,"E0.bottom"),sQuery(id+"F0.wireOp",EDGE,"E0.top"),sQuery(id+"F0.wireOp",EDGE,"E0.left"),sQuery(id+"F0.wireOp",EDGE,"E0.right"),sQuery(id+"F0.wireOp",EDGE,"Jm5Z5nOh-J4Yo-wPLk-m0fh-LtnfEcJKkAPb.bottom"),sQuery(id+"F0.wireOp",EDGE,"Jm5Z5nOh-J4Yo-wPLk-m0fh-LtnfEcJKkAPb.top"),sQuery(id+"F0.wireOp",EDGE,"Jm5Z5nOh-J4Yo-wPLk-m0fh-LtnfEcJKkAPb.left"),sQuery(id+"F0.wireOp",EDGE,"Jm5Z5nOh-J4Yo-wPLk-m0fh-LtnfEcJKkAPb.right"),sQuery(id+"F0.wireOp",EDGE,"E9.bottom"),sQuery(id+"F0.wireOp",EDGE,"E9.top"),sQuery(id+"F0.wireOp",EDGE,"E9.left"),sQuery(id+"F0.wireOp",EDGE,"E9.right"),sQuery(id+"F0.wireOp",EDGE,"4ae19661-8c38-4b12-a6c4-8219772751d5.1.0.1"),sQuery(id+"F0.wireOp",EDGE,"4ae19661-8c38-4b12-a6c4-8219772751d5.1.0.6"),sQuery(id+"F0.wireOp",EDGE,"4ae19661-8c38-4b12-a6c4-8219772751d5.1.0.7"),sQuery(id+"F0.wireOp",EDGE,"4ae19661-8c38-4b12-a6c4-8219772751d5.1.0.8"),sQuery(id+"F0.wireOp",EDGE,"4ae19661-8c38-4b12-a6c4-8219772751d5.1.0.11"),sQuery(id+"F0.wireOp",EDGE,"4ae19661-8c38-4b12-a6c4-8219772751d5.1.0.12"),sQuery(id+"F0.wireOp",EDGE,"4ae19661-8c38-4b12-a6c4-8219772751d5.1.0.13"),sQuery(id+"F0.wireOp",EDGE,"4ae19661-8c38-4b12-a6c4-8219772751d5.1.0.18"),sQuery(id+"F0.wireOp",EDGE,"4ae19661-8c38-4b12-a6c4-8219772751d5.2.0.1"),sQuery(id+"F0.wireOp",EDGE,"4ae19661-8c38-4b12-a6c4-8219772751d5.2.0.6"),sQuery(id+"F0.wireOp",EDGE,"4ae19661-8c38-4b12-a6c4-8219772751d5.2.0.7"),sQuery(id+"F0.wireOp",EDGE,"4ae19661-8c38-4b12-a6c4-8219772751d5.2.0.8"),sQuery(id+"F0.wireOp",EDGE,"4ae19661-8c38-4b12-a6c4-8219772751d5.2.0.11"),sQuery(id+"F0.wireOp",EDGE,"4ae19661-8c38-4b12-a6c4-8219772751d5.2.0.12"),sQuery(id+"F0.wireOp",EDGE,"4ae19661-8c38-4b12-a6c4-8219772751d5.2.0.13"),sQuery(id+"F0.wireOp",EDGE,"4ae19661-8c38-4b12-a6c4-8219772751d5.2.0.18"),sQuery(id+"F0.wireOp",EDGE,"4ae19661-8c38-4b12-a6c4-8219772751d5.3.0.1"),sQuery(id+"F0.wireOp",EDGE,"4ae19661-8c38-4b12-a6c4-8219772751d5.3.0.6"),sQuery(id+"F0.wireOp",EDGE,"4ae19661-8c38-4b12-a6c4-8219772751d5.3.0.7"),sQuery(id+"F0.wireOp",EDGE,"4ae19661-8c38-4b12-a6c4-8219772751d5.3.0.8"),sQuery(id+"F0.wireOp",EDGE,"4ae19661-8c38-4b12-a6c4-8219772751d5.3.0.11"),sQuery(id+"F0.wireOp",EDGE,"4ae19661-8c38-4b12-a6c4-8219772751d5.3.0.12"),sQuery(id+"F0.wireOp",EDGE,"4ae19661-8c38-4b12-a6c4-8219772751d5.3.0.13"),sQuery(id+"F0.wireOp",EDGE,"4ae19661-8c38-4b12-a6c4-8219772751d5.3.0.18"),sQuery(id+"F0.wireOp",EDGE,"4ae19661-8c38-4b12-a6c4-8219772751d5.4.0.1"),sQuery(id+"F0.wireOp",EDGE,"4ae19661-8c38-4b12-a6c4-8219772751d5.4.0.6"),sQuery(id+"F0.wireOp",EDGE,"4ae19661-8c38-4b12-a6c4-8219772751d5.4.0.7"),sQuery(id+"F0.wireOp",EDGE,"4ae19661-8c38-4b12-a6c4-8219772751d5.4.0.8"),sQuery(id+"F0.wireOp",EDGE,"4ae19661-8c38-4b12-a6c4-8219772751d5.4.0.11"),sQuery(id+"F0.wireOp",EDGE,"4ae19661-8c38-4b12-a6c4-8219772751d5.4.0.12"),sQuery(id+"F0.wireOp",EDGE,"4ae19661-8c38-4b12-a6c4-8219772751d5.4.0.13"),sQuery(id+"F0.wireOp",EDGE,"4ae19661-8c38-4b12-a6c4-8219772751d5.4.0.18"),sQuery(id+"F0.wireOp",EDGE,"4ae19661-8c38-4b12-a6c4-8219772751d5.5.0.1"),sQuery(id+"F0.wireOp",EDGE,"4ae19661-8c38-4b12-a6c4-8219772751d5.5.0.6"),sQuery(id+"F0.wireOp",EDGE,"4ae19661-8c38-4b12-a6c4-8219772751d5.5.0.7"),sQuery(id+"F0.wireOp",EDGE,"4ae19661-8c38-4b12-a6c4-8219772751d5.5.0.8"),sQuery(id+"F0.wireOp",EDGE,"4ae19661-8c38-4b12-a6c4-8219772751d5.5.0.11"),sQuery(id+"F0.wireOp",EDGE,"4ae19661-8c38-4b12-a6c4-8219772751d5.5.0.12"),sQuery(id+"F0.wireOp",EDGE,"4ae19661-8c38-4b12-a6c4-8219772751d5.5.0.13"),sQuery(id+"F0.wireOp",EDGE,"4ae19661-8c38-4b12-a6c4-8219772751d5.5.0.18"),sQuery(id+"F0.wireOp",EDGE,"4ae19661-8c38-4b12-a6c4-8219772751d5.6.0.1"),sQuery(id+"F0.wireOp",EDGE,"4ae19661-8c38-4b12-a6c4-8219772751d5.6.0.6"),sQuery(id+"F0.wireOp",EDGE,"4ae19661-8c38-4b12-a6c4-8219772751d5.6.0.7"),sQuery(id+"F0.wireOp",EDGE,"4ae19661-8c38-4b12-a6c4-8219772751d5.6.0.8"),sQuery(id+"F0.wireOp",EDGE,"4ae19661-8c38-4b12-a6c4-8219772751d5.6.0.11"),sQuery(id+"F0.wireOp",EDGE,"4ae19661-8c38-4b12-a6c4-8219772751d5.6.0.12"),sQuery(id+"F0.wireOp",EDGE,"4ae19661-8c38-4b12-a6c4-8219772751d5.6.0.13"),sQuery(id+"F0.wireOp",EDGE,"4ae19661-8c38-4b12-a6c4-8219772751d5.6.0.18"),sQuery(id+"F0.wireOp",EDGE,"4ae19661-8c38-4b12-a6c4-8219772751d5.7.0.1"),sQuery(id+"F0.wireOp",EDGE,"4ae19661-8c38-4b12-a6c4-8219772751d5.7.0.6"),sQuery(id+"F0.wireOp",EDGE,"4ae19661-8c38-4b12-a6c4-8219772751d5.7.0.7"),sQuery(id+"F0.wireOp",EDGE,"4ae19661-8c38-4b12-a6c4-8219772751d5.7.0.8"),sQuery(id+"F0.wireOp",EDGE,"4ae19661-8c38-4b12-a6c4-8219772751d5.7.0.11"),sQuery(id+"F0.wireOp",EDGE,"4ae19661-8c38-4b12-a6c4-8219772751d5.7.0.12"),sQuery(id+"F0.wireOp",EDGE,"4ae19661-8c38-4b12-a6c4-8219772751d5.7.0.13"),sQuery(id+"F0.wireOp",EDGE,"4ae19661-8c38-4b12-a6c4-8219772751d5.7.0.18"),sQuery(id+"F0.wireOp",EDGE,"E10"),sQuery(id+"F0.wireOp",EDGE,"E11"),sQuery(id+"F0.wireOp",EDGE,"E12"),sQuery(id+"F0.wireOp",EDGE,"47ba01c2-e299-4726-b962-d3ee39cc78bc.1.0.1"),sQuery(id+"F0.wireOp",EDGE,"47ba01c2-e299-4726-b962-d3ee39cc78bc.2.0.1"),sQuery(id+"F0.wireOp",EDGE,"47ba01c2-e299-4726-b962-d3ee39cc78bc.3.0.1"),sQuery(id+"F0.wireOp",EDGE,"47ba01c2-e299-4726-b962-d3ee39cc78bc.4.0.1"),sQuery(id+"F0.wireOp",EDGE,"47ba01c2-e299-4726-b962-d3ee39cc78bc.5.0.1"),sQuery(id+"F0.wireOp",EDGE,"47ba01c2-e299-4726-b962-d3ee39cc78bc.6.0.1"),sQuery(id+"F0.wireOp",EDGE,"47ba01c2-e299-4726-b962-d3ee39cc78bc.7.0.1"),sQuery(id+"F0.wireOp",EDGE,"93a5c984-932f-4202-b3e1-f36a6c73e6e3.1.0.1"),sQuery(id+"F0.wireOp",EDGE,"93a5c984-932f-4202-b3e1-f36a6c73e6e3.2.0.1"),sQuery(id+"F0.wireOp",EDGE,"93a5c984-932f-4202-b3e1-f36a6c73e6e3.3.0.1"),sQuery(id+"F0.wireOp",EDGE,"93a5c984-932f-4202-b3e1-f36a6c73e6e3.4.0.1"),sQuery(id+"F0.wireOp",EDGE,"93a5c984-932f-4202-b3e1-f36a6c73e6e3.5.0.1"),sQuery(id+"F0.wireOp",EDGE,"93a5c984-932f-4202-b3e1-f36a6c73e6e3.6.0.1"),sQuery(id+"F0.wireOp",EDGE,"93a5c984-932f-4202-b3e1-f36a6c73e6e3.7.0.1"),sQuery(id+"F0.wireOp",EDGE,"4b779a05-3379-46eb-a5e4-6f14965aae69.1.0.1"),sQuery(id+"F0.wireOp",EDGE,"4b779a05-3379-46eb-a5e4-6f14965aae69.2.0.1"),sQuery(id+"F0.wireOp",EDGE,"4b779a05-3379-46eb-a5e4-6f14965aae69.3.0.1"),sQuery(id+"F0.wireOp",EDGE,"4b779a05-3379-46eb-a5e4-6f14965aae69.4.0.1"),sQuery(id+"F0.wireOp",EDGE,"4b779a05-3379-46eb-a5e4-6f14965aae69.5.0.1"),sQuery(id+"F0.wireOp",EDGE,"4b779a05-3379-46eb-a5e4-6f14965aae69.6.0.1"),sQuery(id+"F0.wireOp",EDGE,"4b779a05-3379-46eb-a5e4-6f14965aae69.7.0.1")])],"isStart":false});
            var sketch = newSketch(context, id + "F2", { "sketchPlane" : qUnion([Q0])});
            skLineSegment(sketch, "E63.bottom", {"start": v(0, 0) * mm, "end": v(100, 0) * mm});
            skLineSegment(sketch, "E63.top", {"start": v(0, -60) * mm, "end": v(100, -60) * mm});
            skLineSegment(sketch, "E63.left", {"start": v(0, 0) * mm, "end": v(0, -60) * mm});
            skLineSegment(sketch, "E63.right", {"start": v(100, 0) * mm, "end": v(100, -60) * mm});
            skLineSegment(sketch, "E64.0", {"start": v(4, -4) * mm, "end": v(96, -4) * mm});
            skLineSegment(sketch, "E64.1", {"start": v(4, -4) * mm, "end": v(4, -56) * mm});
            skLineSegment(sketch, "E64.2", {"start": v(4, -56) * mm, "end": v(96, -56) * mm});
            skLineSegment(sketch, "E64.3", {"start": v(96, -4) * mm, "end": v(96, -56) * mm});
            skLineSegment(sketch, "E65", {"start": v(0, -12) * mm, "end": v(4, -12) * mm});
            skLineSegment(sketch, "E66", {"start": v(19, 0) * mm, "end": v(19, -4) * mm});
            skLineSegment(sketch, "E67", {"start": v(0, -30) * mm, "end": v(4, -30) * mm, "construction": true});
            skLineSegment(sketch, "E68", {"start": v(0, -26) * mm, "end": v(4, -26) * mm});
            skLineSegment(sketch, "E69.MirrorCS", {"start": v(0, -34) * mm, "end": v(4, -34) * mm});
            skLineSegment(sketch, "E70", {"start": v(50, -60) * mm, "end": v(50, 0) * mm, "construction": true});
            skLineSegment(sketch, "E71", {"start": v(45, -56) * mm, "end": v(45, -60) * mm});
            skLineSegment(sketch, "E72.MirrorCS", {"start": v(100, -26) * mm, "end": v(96, -26) * mm});
            skLineSegment(sketch, "E73.MirrorCS", {"start": v(100, -34) * mm, "end": v(96, -34) * mm});
            skLineSegment(sketch, "E74.MirrorCS", {"start": v(100, -12) * mm, "end": v(96, -12) * mm});
            skLineSegment(sketch, "E75.MirrorCS", {"start": v(81, 0) * mm, "end": v(81, -4) * mm});
            skLineSegment(sketch, "E76.MirrorCS", {"start": v(55, -56) * mm, "end": v(55, -60) * mm});
            skLineSegment(sketch, "E77.MirrorCS", {"start": v(0, -48) * mm, "end": v(4, -48) * mm});
            skLineSegment(sketch, "E78.MirrorCS", {"start": v(19, -60) * mm, "end": v(19, -56) * mm});
            skLineSegment(sketch, "E79.MirrorCS", {"start": v(45, -4) * mm, "end": v(45, 0) * mm});
            skLineSegment(sketch, "E80.MirrorCS", {"start": v(55, -4) * mm, "end": v(55, 0) * mm});
            skLineSegment(sketch, "E81.MirrorCS", {"start": v(81, -60) * mm, "end": v(81, -56) * mm});
            skLineSegment(sketch, "E82.MirrorCS", {"start": v(100, -48) * mm, "end": v(96, -48) * mm});
            skCircle(sketch, "E83", {"center": v(10.46, -2) * mm, "radius": 0.5 * mm});
            skPoint(sketch, "E83.centerSnap0", {"position": v(19, -2) * mm});
            skCircle(sketch, "E84.MirrorC", {"center": v(89.54, -2) * mm, "radius": 0.5 * mm});
            skCircle(sketch, "E85.MirrorC", {"center": v(10.46, -58) * mm, "radius": 0.5 * mm});
            skCircle(sketch, "E86.MirrorC", {"center": v(89.54, -58) * mm, "radius": 0.5 * mm});
            skSolve(sketch);
        }
        {
            var Q0;
            Q0=makeQuery(id+"F2.imprint","IMPRINT",FACE,{"disambiguationData":[TD([[makeQuery(id+"F2.imprint","IMPRINT",EDGE,{"derivedFrom":sQuery(id+"F2.wireOp",EDGE,"E86.MirrorC")}),1.0]])]});
            var Q1;
            Q1=makeQuery(id+"F2.imprint","IMPRINT",FACE,{"disambiguationData":[TD([[makeQuery(id+"F2.imprint","IMPRINT",EDGE,{"derivedFrom":sQuery(id+"F2.wireOp",EDGE,"E85.MirrorC")}),-1.0]])]});
            var Q2;
            Q2=makeQuery(id+"F2.imprint","IMPRINT",FACE,{"disambiguationData":[TD([[makeQuery(id+"F2.imprint","IMPRINT",EDGE,{"derivedFrom":sQuery(id+"F2.wireOp",EDGE,"E83")}),1.0]])]});
            var Q3;
            Q3=makeQuery(id+"F2.imprint","IMPRINT",FACE,{"disambiguationData":[TD([[makeQuery(id+"F2.imprint","IMPRINT",EDGE,{"derivedFrom":sQuery(id+"F2.wireOp",EDGE,"E84.MirrorC")}),-1.0]])]});
            extrude(context, id + "F3", {"entities" : qUnion([Q0, Q1, Q2, Q3]), "operationType" : NewBodyOperationType.ADD, "depth" : 8 * mm});
        }
        {
            var Q0;
            {var subQ4=sQuery(id+"F2.wireOp",EDGE,"E74.MirrorCS");Q0=makeQuery(id+"F2.imprint","IMPRINT",FACE,{"disambiguationData":[TD([[makeQuery(id+"F2.imprint","IMPRINT",EDGE,{"derivedFrom":subQ4}),-1.0]])]});}
            var Q1;
            {var subQ0=sQuery(id+"F2.wireOp",EDGE,"E79.MirrorCS");Q1=makeQuery(id+"F2.imprint","IMPRINT",FACE,{"disambiguationData":[TD([[makeQuery(id+"F2.imprint","IMPRINT",EDGE,{"derivedFrom":subQ0}),-1.0]])]});}
            var Q2;
            {var subQ3=sQuery(id+"F2.wireOp",EDGE,"E65");Q2=makeQuery(id+"F2.imprint","IMPRINT",FACE,{"disambiguationData":[TD([[makeQuery(id+"F2.imprint","IMPRINT",EDGE,{"derivedFrom":subQ3}),1.0]])]});}
            var Q3;
            {var subQ0=sQuery(id+"F2.wireOp",EDGE,"E68");Q3=makeQuery(id+"F2.imprint","IMPRINT",FACE,{"disambiguationData":[TD([[makeQuery(id+"F2.imprint","IMPRINT",EDGE,{"derivedFrom":subQ0}),-1.0]])]});}
            var Q4;
            {var subQ3=sQuery(id+"F2.wireOp",EDGE,"E77.MirrorCS");Q4=makeQuery(id+"F2.imprint","IMPRINT",FACE,{"disambiguationData":[TD([[makeQuery(id+"F2.imprint","IMPRINT",EDGE,{"derivedFrom":subQ3}),-1.0]])]});}
            var Q5;
            {var subQ4=sQuery(id+"F2.wireOp",EDGE,"E81.MirrorCS");Q5=makeQuery(id+"F2.imprint","IMPRINT",FACE,{"disambiguationData":[TD([[makeQuery(id+"F2.imprint","IMPRINT",EDGE,{"derivedFrom":subQ4}),-1.0]])]});}
            var Q6;
            {var subQ0=sQuery(id+"F2.wireOp",EDGE,"E72.MirrorCS");Q6=makeQuery(id+"F2.imprint","IMPRINT",FACE,{"disambiguationData":[TD([[makeQuery(id+"F2.imprint","IMPRINT",EDGE,{"derivedFrom":subQ0}),1.0]])]});}
            var Q7;
            {var subQ0=sQuery(id+"F2.wireOp",EDGE,"E71");Q7=makeQuery(id+"F2.imprint","IMPRINT",FACE,{"disambiguationData":[TD([[makeQuery(id+"F2.imprint","IMPRINT",EDGE,{"derivedFrom":subQ0}),1.0]])]});}
            extrude(context, id + "F4", {"entities" : qUnion([Q0, Q1, Q2, Q3, Q4, Q5, Q6, Q7]), "operationType" : NewBodyOperationType.ADD, "depth" : 12 * mm});
        }
        {
            var Q0;
            {var subQ0=sQuery(id+"F2.wireOp",EDGE,"E63.left");Q0=makeQuery(id+"F4.boolean.opBoolean","MERGE",FACE,{"derivedFrom":[makeQuery(id+"F1.opExtrude","SWEPT_FACE",FACE,{"disambiguationData":[OSD([sQuery(id+"F0.wireOp",EDGE,"E0.left")])]}),makeQuery(id+"F4.opExtrude","SWEPT_FACE",FACE,{"disambiguationData":[OSD([subQ0]),TDD([makeQuery(id+"F2.imprint","IMPRINT",EDGE,{"disambiguationData":[TD([[makeQuery(id+"F2.imprint","INTERSECT",VERTEX,{"derivedFrom":[sQuery(id+"F2.wireOp",EDGE,"E63.bottom"),subQ0]}),-1.0]])],"derivedFrom":subQ0})])]}),makeQuery(id+"F4.opExtrude","SWEPT_FACE",FACE,{"disambiguationData":[OSD([subQ0]),TDD([makeQuery(id+"F2.imprint","IMPRINT",EDGE,{"disambiguationData":[TD([[makeQuery(id+"F2.imprint","INTERSECT",VERTEX,{"derivedFrom":[subQ0,sQuery(id+"F2.wireOp",EDGE,"E68")]}),-1.0]])],"derivedFrom":subQ0})])]}),makeQuery(id+"F4.opExtrude","SWEPT_FACE",FACE,{"disambiguationData":[OSD([subQ0]),TDD([makeQuery(id+"F2.imprint","IMPRINT",EDGE,{"disambiguationData":[TD([[makeQuery(id+"F2.imprint","INTERSECT",VERTEX,{"derivedFrom":[sQuery(id+"F2.wireOp",EDGE,"E63.top"),subQ0]}),1.0]])],"derivedFrom":subQ0})])]})]});}
            var sketch = newSketch(context, id + "F5", { "sketchPlane" : qUnion([Q0])});
            skLineSegment(sketch, "E87", {"start": v(-60, -22) * mm, "end": v(0, -19) * mm});
            skLineSegment(sketch, "E88", {"start": v(0, -19) * mm, "end": v(0, -22) * mm});
            skLineSegment(sketch, "E89", {"start": v(0, -22) * mm, "end": v(-60, -22) * mm});
            skSolve(sketch);
        }
        {
            var Q0;
            {var subQ0=sQuery(id+"F5.wireOp",EDGE,"E88");Q0=makeQuery(id+"F5.imprint","IMPRINT",FACE,{"disambiguationData":[TD([[makeQuery(id+"F5.imprint","IMPRINT",EDGE,{"derivedFrom":subQ0}),1.0]])]});}
            var Q1;
            {var subQ0=sQuery(id+"F5.wireOp",EDGE,"E87");var subQ1=sQuery(id+"F2.wireOp",EDGE,"E63.left");var subQ2=makeQuery(id+"F4.opExtrude","SWEPT_EDGE",EDGE,{"disambiguationData":[OSD([subQ1,sQuery(id+"F2.wireOp",EDGE,"E68")])]});var subQ3=makeQuery(id+"F5.imprint","INTERSECT",VERTEX,{"derivedFrom":[subQ2,subQ0]});Q1=makeQuery(id+"F5.imprint","IMPRINT",FACE,{"disambiguationData":[TD([[makeQuery(id+"F5.imprint","IMPRINT",EDGE,{"disambiguationData":[TD([[subQ3,-1.0]])],"derivedFrom":subQ0}),-1.0]])]});}
            var Q2;
            {var subQ0=sQuery(id+"F5.wireOp",EDGE,"E87");var subQ1=sQuery(id+"F2.wireOp",EDGE,"E63.left");var subQ2=makeQuery(id+"F4.opExtrude","SWEPT_EDGE",EDGE,{"disambiguationData":[OSD([subQ1,sQuery(id+"F2.wireOp",EDGE,"E69.MirrorCS")])]});var subQ3=makeQuery(id+"F5.imprint","INTERSECT",VERTEX,{"derivedFrom":[subQ2,subQ0]});Q2=makeQuery(id+"F5.imprint","IMPRINT",FACE,{"disambiguationData":[TD([[makeQuery(id+"F5.imprint","IMPRINT",EDGE,{"disambiguationData":[TD([[subQ3,-1.0]])],"derivedFrom":subQ0}),-1.0]])]});}
            var Q3;
            {var subQ0=sQuery(id+"F5.wireOp",EDGE,"E89");var subQ2=sQuery(id+"F2.wireOp",EDGE,"E63.left");var subQ4=makeQuery(id+"F4.opExtrude","SWEPT_EDGE",EDGE,{"disambiguationData":[OSD([subQ2,sQuery(id+"F2.wireOp",EDGE,"E77.MirrorCS")])]});var subQ6=makeQuery(id+"F5.imprint","INTERSECT",VERTEX,{"derivedFrom":[subQ4,subQ0]});Q3=makeQuery(id+"F5.imprint","IMPRINT",FACE,{"disambiguationData":[TD([[makeQuery(id+"F5.imprint","IMPRINT",EDGE,{"disambiguationData":[TD([[subQ6,-1.0]])],"derivedFrom":subQ4}),1.0]])]});}
            var Q4;
            {var subQ0=sQuery(id+"F5.wireOp",EDGE,"E87");var subQ1=sQuery(id+"F2.wireOp",EDGE,"E63.left");var subQ2=makeQuery(id+"F4.opExtrude","SWEPT_EDGE",EDGE,{"disambiguationData":[OSD([subQ1,sQuery(id+"F2.wireOp",EDGE,"E77.MirrorCS")])]});var subQ3=makeQuery(id+"F5.imprint","INTERSECT",VERTEX,{"derivedFrom":[subQ2,subQ0]});Q4=makeQuery(id+"F5.imprint","IMPRINT",FACE,{"disambiguationData":[TD([[makeQuery(id+"F5.imprint","IMPRINT",EDGE,{"disambiguationData":[TD([[subQ3,-1.0]])],"derivedFrom":subQ0}),-1.0]])]});}
            extrude(context, id + "F6", {"entities" : qUnion([Q0, Q1, Q2, Q3, Q4]), "operationType" : NewBodyOperationType.REMOVE, "oppositeDirection" : true, "depth" : 100 * mm});
        }
        {
            var Q0;
            Q0=makeQuery(id+"F0.imprint","IMPRINT",FACE,{"disambiguationData":[TD([[makeQuery(id+"F0.imprint","IMPRINT",EDGE,{"derivedFrom":sQuery(id+"F0.wireOp",EDGE,"E19.sketch_text.stroke-0")}),-1.0]])]});
            var Q1;
            Q1=makeQuery(id+"F0.imprint","IMPRINT",FACE,{"disambiguationData":[TD([[makeQuery(id+"F0.imprint","IMPRINT",EDGE,{"derivedFrom":sQuery(id+"F0.wireOp",EDGE,"E20.sketch_text.stroke-0")}),-1.0]])]});
            var Q2;
            Q2=makeQuery(id+"F0.imprint","IMPRINT",FACE,{"disambiguationData":[TD([[makeQuery(id+"F0.imprint","IMPRINT",EDGE,{"derivedFrom":sQuery(id+"F0.wireOp",EDGE,"E21.sketch_text.stroke-0")}),-1.0]])]});
            var Q3;
            Q3=makeQuery(id+"F0.imprint","IMPRINT",FACE,{"disambiguationData":[TD([[makeQuery(id+"F0.imprint","IMPRINT",EDGE,{"derivedFrom":sQuery(id+"F0.wireOp",EDGE,"E22.sketch_text.stroke-0")}),-1.0]])]});
            var Q4;
            Q4=makeQuery(id+"F0.imprint","IMPRINT",FACE,{"disambiguationData":[TD([[makeQuery(id+"F0.imprint","IMPRINT",EDGE,{"derivedFrom":sQuery(id+"F0.wireOp",EDGE,"E23.sketch_text.stroke-0")}),-1.0]])]});
            var Q5;
            {var subQ0=sQuery(id+"F0.wireOp",EDGE,"E23.sketch_text.stroke-4");var subQ1=sQuery(id+"F0.wireOp",EDGE,"E4.0");var subQ2=makeQuery(id+"F0.imprint","INTERSECT",VERTEX,{"derivedFrom":[subQ1,subQ0]});Q5=makeQuery(id+"F0.imprint","IMPRINT",FACE,{"disambiguationData":[TD([[makeQuery(id+"F0.imprint","IMPRINT",EDGE,{"disambiguationData":[TD([[subQ2,-1.0]])],"derivedFrom":subQ1}),-1.0]])]});}
            var Q6;
            Q6=makeQuery(id+"F0.imprint","IMPRINT",FACE,{"disambiguationData":[TD([[makeQuery(id+"F0.imprint","IMPRINT",EDGE,{"derivedFrom":sQuery(id+"F0.wireOp",EDGE,"E24.sketch_text.stroke-0")}),-1.0]])]});
            var Q7;
            {var subQ0=sQuery(id+"F0.wireOp",EDGE,"E24.sketch_text.stroke-13");var subQ1=sQuery(id+"F0.wireOp",EDGE,"E4.0");var subQ2=makeQuery(id+"F0.imprint","INTERSECT",VERTEX,{"derivedFrom":[subQ1,subQ0]});Q7=makeQuery(id+"F0.imprint","IMPRINT",FACE,{"disambiguationData":[TD([[makeQuery(id+"F0.imprint","IMPRINT",EDGE,{"disambiguationData":[TD([[subQ2,-1.0]])],"derivedFrom":subQ1}),-1.0]])]});}
            var Q8;
            Q8=makeQuery(id+"F0.imprint","IMPRINT",FACE,{"disambiguationData":[TD([[makeQuery(id+"F0.imprint","IMPRINT",EDGE,{"derivedFrom":sQuery(id+"F0.wireOp",EDGE,"E25.sketch_text.stroke-0")}),-1.0]])]});
            var Q9;
            {var subQ0=sQuery(id+"F0.wireOp",EDGE,"E26.sketch_text.stroke-8");var subQ1=sQuery(id+"F0.wireOp",EDGE,"E4.0");var subQ2=makeQuery(id+"F0.imprint","INTERSECT",VERTEX,{"derivedFrom":[subQ1,subQ0]});Q9=makeQuery(id+"F0.imprint","IMPRINT",FACE,{"disambiguationData":[TD([[makeQuery(id+"F0.imprint","IMPRINT",EDGE,{"disambiguationData":[TD([[subQ2,-1.0]])],"derivedFrom":subQ1}),-1.0]])]});}
            var Q10;
            Q10=makeQuery(id+"F0.imprint","IMPRINT",FACE,{"disambiguationData":[TD([[makeQuery(id+"F0.imprint","IMPRINT",EDGE,{"derivedFrom":sQuery(id+"F0.wireOp",EDGE,"E26.sketch_text.stroke-0")}),-1.0]])]});
            var Q11;
            Q11=makeQuery(id+"F0.imprint","IMPRINT",FACE,{"disambiguationData":[TD([[makeQuery(id+"F0.imprint","IMPRINT",EDGE,{"derivedFrom":sQuery(id+"F0.wireOp",EDGE,"E62.sketch_text.stroke-0")}),-1.0]])]});
            var Q12;
            Q12=makeQuery(id+"F0.imprint","IMPRINT",FACE,{"disambiguationData":[TD([[makeQuery(id+"F0.imprint","IMPRINT",EDGE,{"derivedFrom":sQuery(id+"F0.wireOp",EDGE,"E62.sketch_text.stroke-10")}),-1.0]])]});
            var Q13;
            Q13=makeQuery(id+"F0.imprint","IMPRINT",FACE,{"disambiguationData":[TD([[makeQuery(id+"F0.imprint","IMPRINT",EDGE,{"derivedFrom":sQuery(id+"F0.wireOp",EDGE,"E62.sketch_text.stroke-24")}),-1.0]])]});
            extrude(context, id + "F7", {"entities" : qUnion([Q0, Q1, Q2, Q3, Q4, Q5, Q6, Q7, Q8, Q9, Q10, Q11, Q12, Q13]), "operationType" : NewBodyOperationType.REMOVE, "oppositeDirection" : true, "depth" : 0.8 * mm});
        }
        {
            var Q0;
            Q0=makeQuery(id+"F0.imprint","IMPRINT",FACE,{"disambiguationData":[TD([[makeQuery(id+"F0.imprint","IMPRINT",EDGE,{"derivedFrom":sQuery(id+"F0.wireOp",EDGE,"E6")}),1.0]])]});
            var Q1;
            Q1=makeQuery(id+"F0.imprint","IMPRINT",FACE,{"disambiguationData":[TD([[makeQuery(id+"F0.imprint","IMPRINT",EDGE,{"derivedFrom":sQuery(id+"F0.wireOp",EDGE,"E18.1.0.12")}),-1.0]])]});
            var Q2;
            Q2=makeQuery(id+"F0.imprint","IMPRINT",FACE,{"disambiguationData":[TD([[makeQuery(id+"F0.imprint","IMPRINT",EDGE,{"derivedFrom":sQuery(id+"F0.wireOp",EDGE,"E7")}),1.0]])]});
            var Q3;
            Q3=makeQuery(id+"F0.imprint","IMPRINT",FACE,{"disambiguationData":[TD([[makeQuery(id+"F0.imprint","IMPRINT",EDGE,{"derivedFrom":sQuery(id+"F0.wireOp",EDGE,"E18.1.0.16")}),-1.0]])]});
            var Q4;
            Q4=makeQuery(id+"F0.imprint","IMPRINT",FACE,{"disambiguationData":[TD([[makeQuery(id+"F0.imprint","IMPRINT",EDGE,{"derivedFrom":sQuery(id+"F0.wireOp",EDGE,"E18.2.0.16")}),-1.0]])]});
            var Q5;
            Q5=makeQuery(id+"F0.imprint","IMPRINT",FACE,{"disambiguationData":[TD([[makeQuery(id+"F0.imprint","IMPRINT",EDGE,{"derivedFrom":sQuery(id+"F0.wireOp",EDGE,"E18.3.0.16")}),-1.0]])]});
            var Q6;
            Q6=makeQuery(id+"F0.imprint","IMPRINT",FACE,{"disambiguationData":[TD([[makeQuery(id+"F0.imprint","IMPRINT",EDGE,{"derivedFrom":sQuery(id+"F0.wireOp",EDGE,"E18.3.0.12")}),-1.0]])]});
            var Q7;
            Q7=makeQuery(id+"F0.imprint","IMPRINT",FACE,{"disambiguationData":[TD([[makeQuery(id+"F0.imprint","IMPRINT",EDGE,{"derivedFrom":sQuery(id+"F0.wireOp",EDGE,"E18.2.0.12")}),-1.0]])]});
            var Q8;
            Q8=makeQuery(id+"F0.imprint","IMPRINT",FACE,{"disambiguationData":[TD([[makeQuery(id+"F0.imprint","IMPRINT",EDGE,{"derivedFrom":sQuery(id+"F0.wireOp",EDGE,"E18.4.0.16")}),-1.0]])]});
            var Q9;
            Q9=makeQuery(id+"F0.imprint","IMPRINT",FACE,{"disambiguationData":[TD([[makeQuery(id+"F0.imprint","IMPRINT",EDGE,{"derivedFrom":sQuery(id+"F0.wireOp",EDGE,"E18.4.0.12")}),-1.0]])]});
            var Q10;
            Q10=makeQuery(id+"F0.imprint","IMPRINT",FACE,{"disambiguationData":[TD([[makeQuery(id+"F0.imprint","IMPRINT",EDGE,{"derivedFrom":sQuery(id+"F0.wireOp",EDGE,"E18.5.0.16")}),-1.0]])]});
            var Q11;
            Q11=makeQuery(id+"F0.imprint","IMPRINT",FACE,{"disambiguationData":[TD([[makeQuery(id+"F0.imprint","IMPRINT",EDGE,{"derivedFrom":sQuery(id+"F0.wireOp",EDGE,"E18.6.0.16")}),-1.0]])]});
            var Q12;
            Q12=makeQuery(id+"F0.imprint","IMPRINT",FACE,{"disambiguationData":[TD([[makeQuery(id+"F0.imprint","IMPRINT",EDGE,{"derivedFrom":sQuery(id+"F0.wireOp",EDGE,"E18.5.0.12")}),-1.0]])]});
            var Q13;
            Q13=makeQuery(id+"F0.imprint","IMPRINT",FACE,{"disambiguationData":[TD([[makeQuery(id+"F0.imprint","IMPRINT",EDGE,{"derivedFrom":sQuery(id+"F0.wireOp",EDGE,"E18.6.0.12")}),-1.0]])]});
            var Q14;
            Q14=makeQuery(id+"F0.imprint","IMPRINT",FACE,{"disambiguationData":[TD([[makeQuery(id+"F0.imprint","IMPRINT",EDGE,{"derivedFrom":sQuery(id+"F0.wireOp",EDGE,"E18.7.0.16")}),-1.0]])]});
            var Q15;
            Q15=makeQuery(id+"F0.imprint","IMPRINT",FACE,{"disambiguationData":[TD([[makeQuery(id+"F0.imprint","IMPRINT",EDGE,{"derivedFrom":sQuery(id+"F0.wireOp",EDGE,"E18.7.0.12")}),-1.0]])]});
            var Q16;
            Q16=makeQuery(id+"F0.imprint","IMPRINT",FACE,{"disambiguationData":[TD([[makeQuery(id+"F0.imprint","IMPRINT",EDGE,{"derivedFrom":sQuery(id+"F0.wireOp",EDGE,"E60.bottom")}),-1.0]])]});
            var Q17;
            Q17=makeQuery(id+"F0.imprint","IMPRINT",FACE,{"disambiguationData":[TD([[makeQuery(id+"F0.imprint","IMPRINT",EDGE,{"derivedFrom":sQuery(id+"F0.wireOp",EDGE,"E58.bottom")}),-1.0]])]});
            var Q18;
            Q18=makeQuery(id+"F0.imprint","IMPRINT",FACE,{"disambiguationData":[TD([[makeQuery(id+"F0.imprint","IMPRINT",EDGE,{"derivedFrom":sQuery(id+"F0.wireOp",EDGE,"E18.1.0.6")}),1.0]])]});
            var Q19;
            Q19=makeQuery(id+"F0.imprint","IMPRINT",FACE,{"disambiguationData":[TD([[makeQuery(id+"F0.imprint","IMPRINT",EDGE,{"derivedFrom":sQuery(id+"F0.wireOp",EDGE,"E15.bottom")}),-1.0]])]});
            var Q20;
            Q20=makeQuery(id+"F0.imprint","IMPRINT",FACE,{"disambiguationData":[TD([[makeQuery(id+"F0.imprint","IMPRINT",EDGE,{"derivedFrom":sQuery(id+"F0.wireOp",EDGE,"E3")}),1.0]])]});
            var Q21;
            Q21=makeQuery(id+"F0.imprint","IMPRINT",FACE,{"disambiguationData":[TD([[makeQuery(id+"F0.imprint","IMPRINT",EDGE,{"derivedFrom":sQuery(id+"F0.wireOp",EDGE,"E8.bottom")}),1.0]])]});
            var Q22;
            Q22=makeQuery(id+"F0.imprint","IMPRINT",FACE,{"disambiguationData":[TD([[makeQuery(id+"F0.imprint","IMPRINT",EDGE,{"derivedFrom":sQuery(id+"F0.wireOp",EDGE,"E18.1.0.0")}),1.0]])]});
            var Q23;
            Q23=makeQuery(id+"F0.imprint","IMPRINT",FACE,{"disambiguationData":[TD([[makeQuery(id+"F0.imprint","IMPRINT",EDGE,{"derivedFrom":sQuery(id+"F0.wireOp",EDGE,"E18.2.0.2")}),1.0]])]});
            var Q24;
            Q24=makeQuery(id+"F0.imprint","IMPRINT",FACE,{"disambiguationData":[TD([[makeQuery(id+"F0.imprint","IMPRINT",EDGE,{"derivedFrom":sQuery(id+"F0.wireOp",EDGE,"E18.1.0.2")}),1.0]])]});
            var Q25;
            Q25=makeQuery(id+"F0.imprint","IMPRINT",FACE,{"disambiguationData":[TD([[makeQuery(id+"F0.imprint","IMPRINT",EDGE,{"derivedFrom":sQuery(id+"F0.wireOp",EDGE,"E18.2.0.0")}),1.0]])]});
            var Q26;
            Q26=makeQuery(id+"F0.imprint","IMPRINT",FACE,{"disambiguationData":[TD([[makeQuery(id+"F0.imprint","IMPRINT",EDGE,{"derivedFrom":sQuery(id+"F0.wireOp",EDGE,"E18.3.0.0")}),1.0]])]});
            var Q27;
            Q27=makeQuery(id+"F0.imprint","IMPRINT",FACE,{"disambiguationData":[TD([[makeQuery(id+"F0.imprint","IMPRINT",EDGE,{"derivedFrom":sQuery(id+"F0.wireOp",EDGE,"E18.3.0.2")}),1.0]])]});
            var Q28;
            Q28=makeQuery(id+"F0.imprint","IMPRINT",FACE,{"disambiguationData":[TD([[makeQuery(id+"F0.imprint","IMPRINT",EDGE,{"derivedFrom":sQuery(id+"F0.wireOp",EDGE,"E18.4.0.0")}),1.0]])]});
            var Q29;
            Q29=makeQuery(id+"F0.imprint","IMPRINT",FACE,{"disambiguationData":[TD([[makeQuery(id+"F0.imprint","IMPRINT",EDGE,{"derivedFrom":sQuery(id+"F0.wireOp",EDGE,"E18.4.0.2")}),1.0]])]});
            var Q30;
            Q30=makeQuery(id+"F0.imprint","IMPRINT",FACE,{"disambiguationData":[TD([[makeQuery(id+"F0.imprint","IMPRINT",EDGE,{"derivedFrom":sQuery(id+"F0.wireOp",EDGE,"E18.4.0.6")}),1.0]])]});
            var Q31;
            Q31=makeQuery(id+"F0.imprint","IMPRINT",FACE,{"disambiguationData":[TD([[makeQuery(id+"F0.imprint","IMPRINT",EDGE,{"derivedFrom":sQuery(id+"F0.wireOp",EDGE,"E18.3.0.6")}),1.0]])]});
            var Q32;
            Q32=makeQuery(id+"F0.imprint","IMPRINT",FACE,{"disambiguationData":[TD([[makeQuery(id+"F0.imprint","IMPRINT",EDGE,{"derivedFrom":sQuery(id+"F0.wireOp",EDGE,"E18.2.0.6")}),1.0]])]});
            var Q33;
            Q33=makeQuery(id+"F0.imprint","IMPRINT",FACE,{"disambiguationData":[TD([[makeQuery(id+"F0.imprint","IMPRINT",EDGE,{"derivedFrom":sQuery(id+"F0.wireOp",EDGE,"E18.5.0.6")}),1.0]])]});
            var Q34;
            Q34=makeQuery(id+"F0.imprint","IMPRINT",FACE,{"disambiguationData":[TD([[makeQuery(id+"F0.imprint","IMPRINT",EDGE,{"derivedFrom":sQuery(id+"F0.wireOp",EDGE,"E18.6.0.6")}),1.0]])]});
            var Q35;
            Q35=makeQuery(id+"F0.imprint","IMPRINT",FACE,{"disambiguationData":[TD([[makeQuery(id+"F0.imprint","IMPRINT",EDGE,{"derivedFrom":sQuery(id+"F0.wireOp",EDGE,"E18.5.0.2")}),1.0]])]});
            var Q36;
            Q36=makeQuery(id+"F0.imprint","IMPRINT",FACE,{"disambiguationData":[TD([[makeQuery(id+"F0.imprint","IMPRINT",EDGE,{"derivedFrom":sQuery(id+"F0.wireOp",EDGE,"E18.6.0.2")}),1.0]])]});
            var Q37;
            Q37=makeQuery(id+"F0.imprint","IMPRINT",FACE,{"disambiguationData":[TD([[makeQuery(id+"F0.imprint","IMPRINT",EDGE,{"derivedFrom":sQuery(id+"F0.wireOp",EDGE,"E18.7.0.2")}),1.0]])]});
            var Q38;
            Q38=makeQuery(id+"F0.imprint","IMPRINT",FACE,{"disambiguationData":[TD([[makeQuery(id+"F0.imprint","IMPRINT",EDGE,{"derivedFrom":sQuery(id+"F0.wireOp",EDGE,"E54.bottom")}),-1.0]])]});
            var Q39;
            Q39=makeQuery(id+"F0.imprint","IMPRINT",FACE,{"disambiguationData":[TD([[makeQuery(id+"F0.imprint","IMPRINT",EDGE,{"derivedFrom":sQuery(id+"F0.wireOp",EDGE,"E18.7.0.6")}),1.0]])]});
            var Q40;
            Q40=makeQuery(id+"F0.imprint","IMPRINT",FACE,{"disambiguationData":[TD([[makeQuery(id+"F0.imprint","IMPRINT",EDGE,{"derivedFrom":sQuery(id+"F0.wireOp",EDGE,"E18.5.0.0")}),1.0]])]});
            var Q41;
            Q41=makeQuery(id+"F0.imprint","IMPRINT",FACE,{"disambiguationData":[TD([[makeQuery(id+"F0.imprint","IMPRINT",EDGE,{"derivedFrom":sQuery(id+"F0.wireOp",EDGE,"E56.bottom")}),-1.0]])]});
            var Q42;
            Q42=makeQuery(id+"F0.imprint","IMPRINT",FACE,{"disambiguationData":[TD([[makeQuery(id+"F0.imprint","IMPRINT",EDGE,{"derivedFrom":sQuery(id+"F0.wireOp",EDGE,"E18.7.0.0")}),1.0]])]});
            var Q43;
            Q43=makeQuery(id+"F0.imprint","IMPRINT",FACE,{"disambiguationData":[TD([[makeQuery(id+"F0.imprint","IMPRINT",EDGE,{"derivedFrom":sQuery(id+"F0.wireOp",EDGE,"E18.6.0.0")}),1.0]])]});
            var Q44;
            Q44=makeQuery(id+"F0.imprint","IMPRINT",FACE,{"disambiguationData":[TD([[makeQuery(id+"F0.imprint","IMPRINT",EDGE,{"derivedFrom":sQuery(id+"F0.wireOp",EDGE,"E52.bottom")}),-1.0]])]});
            extrude(context, id + "F8", {"entities" : qUnion([Q0, Q1, Q2, Q3, Q4, Q5, Q6, Q7, Q8, Q9, Q10, Q11, Q12, Q13, Q14, Q15, Q16, Q17, Q18, Q19, Q20, Q21, Q22, Q23, Q24, Q25, Q26, Q27, Q28, Q29, Q30, Q31, Q32, Q33, Q34, Q35, Q36, Q37, Q38, Q39, Q40, Q41, Q42, Q43, Q44]), "operationType" : NewBodyOperationType.REMOVE, "oppositeDirection" : true, "depth" : 5 * mm});
        }
    });
